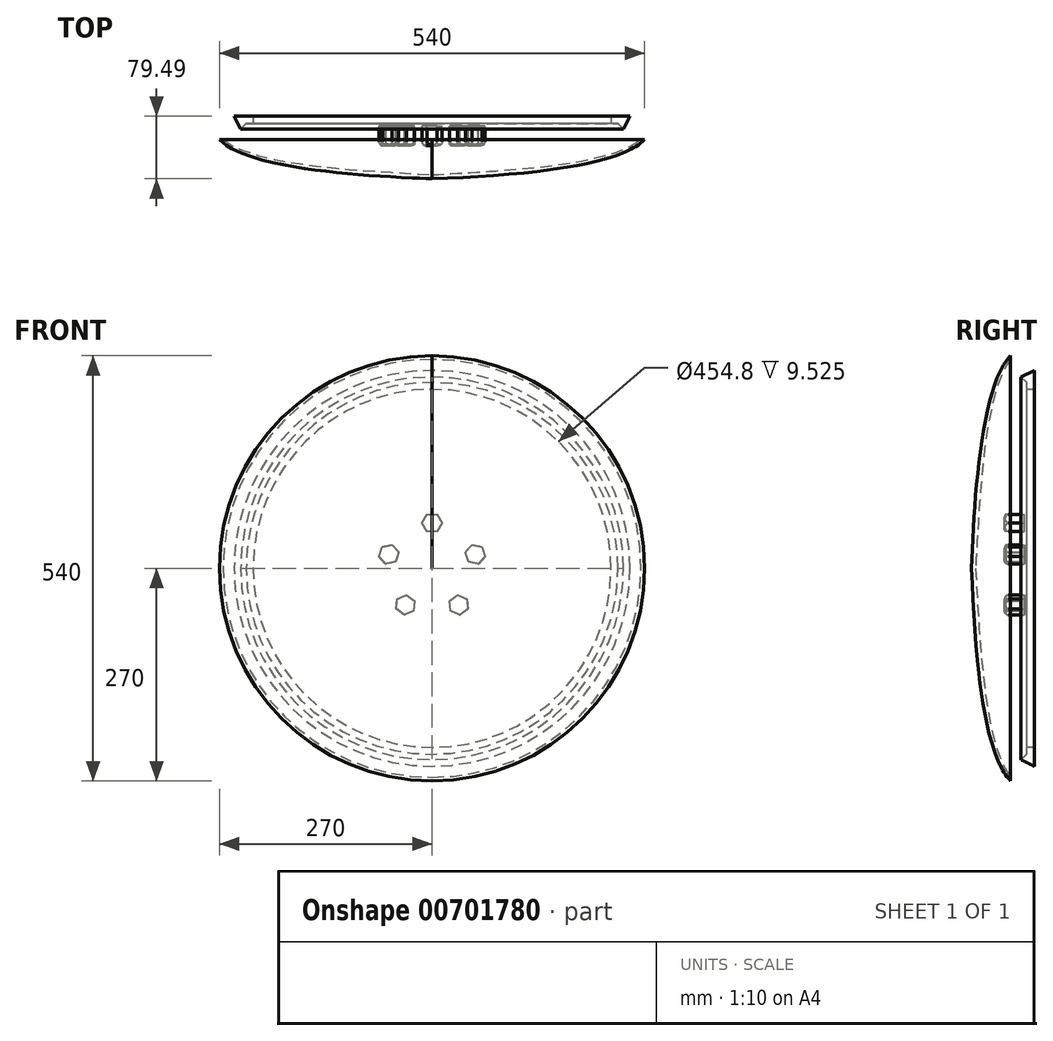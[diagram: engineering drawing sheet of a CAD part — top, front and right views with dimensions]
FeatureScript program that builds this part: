
annotation { "Feature Type Name" : "Feature", "Feature Type Description" : "" }
export const myFeature = defineFeature(function(context is Context, id is Id, definition is map)
    precondition{}
    {
        {
            var Q0;
            Q0=qCreatedBy(makeId("Right.planeOp"),FACE);
            var sketch = newSketch(context, id + "F0", { "sketchPlane" : qUnion([Q0])});
            skLineSegment(sketch, "E0", {"start": v(-492.36, 0) * mm, "end": v(495.3, 0) * mm, "construction": true});
            skLineSegment(sketch, "E1", {"start": v(0, 375.13) * mm, "end": v(0, -370.11) * mm, "construction": true});
            skLineSegment(sketch, "E2", {"start": v(-208.2, 270) * mm, "end": v(-199.87, 270) * mm});
            skLineSegment(sketch, "E3", {"start": v(-208.2, 270) * mm, "end": v(-208.2, 265.42) * mm});
            skLineSegment(sketch, "E4", {"start": v(-208.2, 265.42) * mm, "end": v(-200.05, 260.68) * mm});
            skLineSegment(sketch, "E5", {"start": v(-199.87, 270) * mm, "end": v(-187.28, 253.15) * mm});
            skLineSegment(sketch, "E6", {"start": v(-187.28, 253.15) * mm, "end": v(0, 253.15) * mm});
            skLineSegment(sketch, "E7", {"start": v(-200.05, 260.68) * mm, "end": v(-200.05, 247) * mm});
            skLineSegment(sketch, "E8", {"start": v(-200.05, 247) * mm, "end": v(-212.9, 237.4) * mm});
            skFitSpline(sketch, "E9", {"points": [v(-212.9, 237.4) * mm, v(-223.98, 98.87) * mm], "startDerivative": vector(-18.19, -11.12) * mm, "endDerivative": vector(-3.6, -383.35) * mm});
            skFitSpline(sketch, "E10", {"points": [v(-223.98, 98.87) * mm, v(-190, 0) * mm], "startDerivative": vector(-2.79, -53.63) * mm, "endDerivative": vector(-2.72, -261.66) * mm});
            skLineSegment(sketch, "E11", {"start": v(0, 245.77) * mm, "end": v(-188.8, 245.77) * mm});
            skFitSpline(sketch, "E12", {"points": [v(-188.8, 245.77) * mm, v(-188.8, 102.31) * mm], "startDerivative": vector(-99.7, -5.27) * mm, "endDerivative": vector(28.6, -46.07) * mm});
            skFitSpline(sketch, "E13", {"points": [v(-188.8, 102.31) * mm, v(-128.64, 85.7) * mm], "startDerivative": vector(31.05, -59.65) * mm, "endDerivative": vector(99.06, -4.24) * mm});
            skLineSegment(sketch, "E14.MirrorCS", {"start": v(187.28, 253.15) * mm, "end": v(0, 253.15) * mm});
            skLineSegment(sketch, "E15.MirrorCS", {"start": v(0, 245.77) * mm, "end": v(188.8, 245.77) * mm});
            skLineSegment(sketch, "E16.MirrorCS", {"start": v(199.87, 270) * mm, "end": v(187.28, 253.15) * mm});
            skLineSegment(sketch, "E17.MirrorCS", {"start": v(208.2, 270) * mm, "end": v(199.87, 270) * mm});
            skLineSegment(sketch, "E18.MirrorCS", {"start": v(208.2, 270) * mm, "end": v(208.2, 265.42) * mm});
            skLineSegment(sketch, "E19", {"start": v(208.2, 265.42) * mm, "end": v(192.74, 245.77) * mm});
            skLineSegment(sketch, "E20", {"start": v(192.74, 245.77) * mm, "end": v(188.8, 245.77) * mm});
            skLineSegment(sketch, "E21", {"start": v(-128.64, 85.7) * mm, "end": v(-128.64, 0) * mm});
            skLineSegment(sketch, "E22", {"start": v(-128.64, 0) * mm, "end": v(-190, 0) * mm});
            skSolve(sketch);
        }
        {
            var Q0;
            Q0 = qSketchRegion(id + "F0", true);
            var Q1;
            Q1=sQuery(id+"F0.wireOp",EDGE,"E0");
            revolve(context, id + "F1", {"entities" : qUnion([Q0]), "axis" : qUnion([Q1]), "revolveType" : RevolveType.FULL});
        }
        {
            var Q0;
            Q0=qCreatedBy(makeId("Front.planeOp"),FACE);
            cPlane(context, id + "F2", {"entities" : qUnion([Q0]), "cplaneType" : CPlaneType.OFFSET, "offset" : 230 * mm, "width" : 150 * mm, "height" : 150 * mm});
        }
        {
            var Q0;
            Q0=qCreatedBy(id+"F2.planeOp",FACE);
            var sketch = newSketch(context, id + "F3", { "sketchPlane" : qUnion([Q0])});
            skLineSegment(sketch, "E23", {"start": v(0, 0) * mm, "end": v(0, 316.28) * mm, "construction": true});
            skArc(sketch, "E24", {"start": v(-3.8, 244.37) * mm, "mid": v(-6.72, 170.75) * mm, "end": v(-5.1, 97.1) * mm});
            skArc(sketch, "E25.MirrorCS", {"start": v(3.8, 244.37) * mm, "mid": v(6.72, 170.75) * mm, "end": v(5.1, 97.1) * mm});
            skArc(sketch, "E26", {"start": v(3.8, 244.37) * mm, "mid": v(0, 248.44) * mm, "end": v(-3.8, 244.37) * mm});
            skArc(sketch, "E27", {"start": v(-5.1, 97.1) * mm, "mid": v(0, 92.54) * mm, "end": v(5.1, 97.1) * mm});
            skLineSegment(sketch, "E28", {"start": v(0, 0) * mm, "end": v(-180.56, 248.53) * mm, "construction": true});
            skArc(sketch, "E29", {"start": v(-147.8, 195.5) * mm, "mid": v(-103.99, 129.86) * mm, "end": v(-55.27, 67.78) * mm});
            skArc(sketch, "E30.MirrorCS", {"start": v(-140.25, 200.98) * mm, "mid": v(-91.37, 139.03) * mm, "end": v(-47.38, 73.51) * mm});
            skArc(sketch, "E31", {"start": v(-140.25, 200.98) * mm, "mid": v(-146.94, 202.25) * mm, "end": v(-147.8, 195.5) * mm});
            skArc(sketch, "E32", {"start": v(-55.27, 67.78) * mm, "mid": v(-48.36, 66.56) * mm, "end": v(-47.38, 73.51) * mm});
            skArc(sketch, "E33.1.0", {"start": v(-233.58, 71.9) * mm, "mid": v(-164.47, 46.37) * mm, "end": v(-93.93, 25.16) * mm});
            skArc(sketch, "E33.1.1", {"start": v(-231.23, 79.12) * mm, "mid": v(-236.28, 76.77) * mm, "end": v(-233.58, 71.9) * mm});
            skArc(sketch, "E33.1.2", {"start": v(-231.23, 79.12) * mm, "mid": v(-160.32, 59.16) * mm, "end": v(-90.77, 34.85) * mm});
            skArc(sketch, "E33.1.3", {"start": v(-93.93, 25.16) * mm, "mid": v(-88, 28.6) * mm, "end": v(-90.77, 34.85) * mm});
            skArc(sketch, "E33.1.4", {"start": v(-81.54, -31.62) * mm, "mid": v(-78.25, -25.42) * mm, "end": v(-84.56, -22.35) * mm});
            skArc(sketch, "E33.1.5", {"start": v(-231.6, -80.15) * mm, "mid": v(-155.64, -58.77) * mm, "end": v(-81.54, -31.62) * mm});
            skArc(sketch, "E33.1.6", {"start": v(-234.48, -71.28) * mm, "mid": v(-160.46, -43.94) * mm, "end": v(-84.56, -22.35) * mm});
            skArc(sketch, "E33.1.7", {"start": v(-234.48, -71.28) * mm, "mid": v(-237.76, -77.25) * mm, "end": v(-231.6, -80.15) * mm});
            skArc(sketch, "E33.2.0", {"start": v(-140.56, -199.93) * mm, "mid": v(-94.93, -142.1) * mm, "end": v(-52.95, -81.55) * mm});
            skArc(sketch, "E33.2.1", {"start": v(-146.7, -195.47) * mm, "mid": v(-146.03, -200.99) * mm, "end": v(-140.56, -199.93) * mm});
            skArc(sketch, "E33.2.2", {"start": v(-146.7, -195.47) * mm, "mid": v(-105.8, -134.2) * mm, "end": v(-61.2, -75.56) * mm});
            skArc(sketch, "E33.2.3", {"start": v(-52.95, -81.55) * mm, "mid": v(-54.4, -74.86) * mm, "end": v(-61.2, -75.56) * mm});
            skArc(sketch, "E33.2.4", {"start": v(4.88, -87.32) * mm, "mid": v(0, -82.28) * mm, "end": v(-4.88, -87.32) * mm});
            skArc(sketch, "E33.2.5", {"start": v(4.66, -245.03) * mm, "mid": v(7.8, -166.18) * mm, "end": v(4.88, -87.32) * mm});
            skArc(sketch, "E33.2.6", {"start": v(-4.66, -245.03) * mm, "mid": v(-7.8, -166.18) * mm, "end": v(-4.88, -87.32) * mm});
            skArc(sketch, "E33.2.7", {"start": v(-4.66, -245.03) * mm, "mid": v(0, -250) * mm, "end": v(4.66, -245.03) * mm});
            skArc(sketch, "E33.3.0", {"start": v(146.7, -195.47) * mm, "mid": v(105.8, -134.2) * mm, "end": v(61.2, -75.56) * mm});
            skArc(sketch, "E33.3.1", {"start": v(140.56, -199.93) * mm, "mid": v(146.03, -200.99) * mm, "end": v(146.7, -195.47) * mm});
            skArc(sketch, "E33.3.2", {"start": v(140.56, -199.93) * mm, "mid": v(94.93, -142.1) * mm, "end": v(52.95, -81.55) * mm});
            skArc(sketch, "E33.3.3", {"start": v(61.2, -75.56) * mm, "mid": v(54.4, -74.86) * mm, "end": v(52.95, -81.55) * mm});
            skArc(sketch, "E33.3.4", {"start": v(84.56, -22.35) * mm, "mid": v(78.25, -25.42) * mm, "end": v(81.54, -31.62) * mm});
            skArc(sketch, "E33.3.5", {"start": v(234.48, -71.28) * mm, "mid": v(160.46, -43.94) * mm, "end": v(84.56, -22.35) * mm});
            skArc(sketch, "E33.3.6", {"start": v(231.6, -80.15) * mm, "mid": v(155.64, -58.77) * mm, "end": v(81.54, -31.62) * mm});
            skArc(sketch, "E33.3.7", {"start": v(231.6, -80.15) * mm, "mid": v(237.76, -77.25) * mm, "end": v(234.48, -71.28) * mm});
            skArc(sketch, "E33.4.0", {"start": v(231.23, 79.12) * mm, "mid": v(160.32, 59.16) * mm, "end": v(90.77, 34.85) * mm});
            skArc(sketch, "E33.4.1", {"start": v(233.58, 71.9) * mm, "mid": v(236.28, 76.77) * mm, "end": v(231.23, 79.12) * mm});
            skArc(sketch, "E33.4.2", {"start": v(233.58, 71.9) * mm, "mid": v(164.47, 46.37) * mm, "end": v(93.93, 25.16) * mm});
            skArc(sketch, "E33.4.3", {"start": v(90.77, 34.85) * mm, "mid": v(88, 28.6) * mm, "end": v(93.93, 25.16) * mm});
            skArc(sketch, "E33.4.4", {"start": v(47.38, 73.51) * mm, "mid": v(48.36, 66.56) * mm, "end": v(55.27, 67.78) * mm});
            skArc(sketch, "E33.4.5", {"start": v(140.25, 200.98) * mm, "mid": v(91.37, 139.03) * mm, "end": v(47.38, 73.51) * mm});
            skArc(sketch, "E33.4.6", {"start": v(147.8, 195.5) * mm, "mid": v(103.99, 129.86) * mm, "end": v(55.27, 67.78) * mm});
            skArc(sketch, "E33.4.7", {"start": v(147.8, 195.5) * mm, "mid": v(146.94, 202.25) * mm, "end": v(140.25, 200.98) * mm});
            skPoint(sketch, "E33.center", {"position": v(0, 0) * mm});
            skSolve(sketch);
        }
        {
            var Q0;
            Q0 = qSketchRegion(id + "F3", true);
            extrude(context, id + "F4", {"entities" : qUnion([Q0]), "operationType" : NewBodyOperationType.REMOVE, "oppositeDirection" : true, "depth" : 46 * mm, "offsetDistance" : 25 * mm, "symmetric" : true});
        }
        {
            var Q0;
            Q0=qCreatedBy(makeId("Right.planeOp"),FACE);
            var sketch = newSketch(context, id + "F5", { "sketchPlane" : qUnion([Q0])});
            skFitSpline(sketch, "E34", {"points": [v(-219.3, 99.24) * mm, v(-211.26, 234.91) * mm], "startDerivative": vector(2.2, 123.97) * mm, "endDerivative": vector(26.33, 34.01) * mm});
            skLineSegment(sketch, "E35", {"start": v(-211.26, 234.91) * mm, "end": v(-194.07, 247.35) * mm});
            skFitSpline(sketch, "E36", {"points": [v(-219.3, 99.24) * mm, v(-188.84, 45.36) * mm], "startDerivative": vector(0.06, -33.78) * mm, "endDerivative": vector(11.74, -109.6) * mm});
            skFitSpline(sketch, "E37", {"points": [v(-188.84, 45.36) * mm, v(-194.07, 247.35) * mm], "startDerivative": vector(-5.23, 201.99) * mm, "endDerivative": vector(97.82, 84.09) * mm});
            skSolve(sketch);
        }
        {
            var Q0;
            Q0 = qSketchRegion(id + "F5", true);
            var Q1;
            Q1=sQuery(id+"F0.wireOp",EDGE,"E0");
            revolve(context, id + "F6", {"operationType" : NewBodyOperationType.ADD, "entities" : qUnion([Q0]), "axis" : qUnion([Q1]), "revolveType" : RevolveType.FULL});
        }
        {
            var Q0;
            Q0=makeQuery(id+"F1.opRevolve","SWEPT_FACE",FACE,{"disambiguationData":[OSD([sQuery(id+"F0.wireOp",EDGE,"E3")])]});
            var sketch = newSketch(context, id + "F7", { "sketchPlane" : qUnion([Q0])});
            skLineSegment(sketch, "E38", {"start": v(0, 0) * mm, "end": v(-101.12, 311.2) * mm, "construction": true});
            skLineSegment(sketch, "E39", {"start": v(0, 314.55) * mm, "end": v(0, -288.55) * mm, "construction": true});
            skArc(sketch, "E40", {"start": v(-118.5, 213.52) * mm, "mid": v(-123.32, 205.59) * mm, "end": v(-121.43, 196.51) * mm});
            skArc(sketch, "E41.MirrorCS", {"start": v(-29.63, 242.4) * mm, "mid": v(-21.08, 238.8) * mm, "end": v(-17.26, 230.36) * mm});
            skArc(sketch, "E42", {"start": v(-39.91, 91.58) * mm, "mid": v(-28.7, 88.34) * mm, "end": v(-21.54, 97.55) * mm});
            skArc(sketch, "E43", {"start": v(-118.5, 213.52) * mm, "mid": v(-75.46, 232.25) * mm, "end": v(-29.63, 242.4) * mm});
            skLineSegment(sketch, "E44", {"start": v(-121.43, 196.51) * mm, "end": v(-39.91, 91.58) * mm});
            skLineSegment(sketch, "E45", {"start": v(-17.26, 230.36) * mm, "end": v(-21.54, 97.55) * mm});
            skArc(sketch, "E46.1.0", {"start": v(-221.38, 103.08) * mm, "mid": v(-197.56, 143.54) * mm, "end": v(-166.45, 178.69) * mm});
            skArc(sketch, "E46.1.1", {"start": v(-166.45, 178.69) * mm, "mid": v(-157.42, 180.81) * mm, "end": v(-149.37, 176.22) * mm});
            skLineSegment(sketch, "E46.1.2", {"start": v(-149.37, 176.22) * mm, "end": v(-74.77, 66.26) * mm});
            skArc(sketch, "E46.1.3", {"start": v(-86.12, 50.63) * mm, "mid": v(-75.15, 54.6) * mm, "end": v(-74.77, 66.26) * mm});
            skLineSegment(sketch, "E46.1.4", {"start": v(-213.75, 87.6) * mm, "end": v(-86.12, 50.63) * mm});
            skArc(sketch, "E46.1.5", {"start": v(-221.38, 103.08) * mm, "mid": v(-220.6, 93.84) * mm, "end": v(-213.75, 87.6) * mm});
            skArc(sketch, "E46.2.0", {"start": v(-239.69, -46.73) * mm, "mid": v(-244.2, 0) * mm, "end": v(-239.69, 46.73) * mm});
            skArc(sketch, "E46.2.1", {"start": v(-239.69, 46.73) * mm, "mid": v(-233.63, 53.75) * mm, "end": v(-224.42, 54.77) * mm});
            skLineSegment(sketch, "E46.2.2", {"start": v(-224.42, 54.77) * mm, "end": v(-99.43, 9.66) * mm});
            skArc(sketch, "E46.2.3", {"start": v(-99.43, -9.66) * mm, "mid": v(-92.88, 0) * mm, "end": v(-99.43, 9.66) * mm});
            skLineSegment(sketch, "E46.2.4", {"start": v(-224.42, -54.77) * mm, "end": v(-99.43, -9.66) * mm});
            skArc(sketch, "E46.2.5", {"start": v(-239.69, -46.73) * mm, "mid": v(-233.63, -53.75) * mm, "end": v(-224.42, -54.77) * mm});
            skArc(sketch, "E46.3.0", {"start": v(-166.45, -178.69) * mm, "mid": v(-197.56, -143.54) * mm, "end": v(-221.38, -103.08) * mm});
            skArc(sketch, "E46.3.1", {"start": v(-221.38, -103.08) * mm, "mid": v(-220.6, -93.84) * mm, "end": v(-213.75, -87.6) * mm});
            skLineSegment(sketch, "E46.3.2", {"start": v(-213.75, -87.6) * mm, "end": v(-86.12, -50.63) * mm});
            skArc(sketch, "E46.3.3", {"start": v(-74.77, -66.26) * mm, "mid": v(-75.15, -54.6) * mm, "end": v(-86.12, -50.63) * mm});
            skLineSegment(sketch, "E46.3.4", {"start": v(-149.37, -176.22) * mm, "end": v(-74.77, -66.26) * mm});
            skArc(sketch, "E46.3.5", {"start": v(-166.45, -178.69) * mm, "mid": v(-157.42, -180.81) * mm, "end": v(-149.37, -176.22) * mm});
            skArc(sketch, "E46.4.0", {"start": v(-29.63, -242.4) * mm, "mid": v(-75.46, -232.25) * mm, "end": v(-118.5, -213.52) * mm});
            skArc(sketch, "E46.4.1", {"start": v(-118.5, -213.52) * mm, "mid": v(-123.32, -205.59) * mm, "end": v(-121.43, -196.51) * mm});
            skLineSegment(sketch, "E46.4.2", {"start": v(-121.43, -196.51) * mm, "end": v(-39.91, -91.58) * mm});
            skArc(sketch, "E46.4.3", {"start": v(-21.54, -97.55) * mm, "mid": v(-28.7, -88.34) * mm, "end": v(-39.91, -91.58) * mm});
            skLineSegment(sketch, "E46.4.4", {"start": v(-17.26, -230.36) * mm, "end": v(-21.54, -97.55) * mm});
            skArc(sketch, "E46.4.5", {"start": v(-29.63, -242.4) * mm, "mid": v(-21.08, -238.8) * mm, "end": v(-17.26, -230.36) * mm});
            skArc(sketch, "E46.5.0", {"start": v(118.5, -213.52) * mm, "mid": v(75.46, -232.25) * mm, "end": v(29.63, -242.4) * mm});
            skArc(sketch, "E46.5.1", {"start": v(29.63, -242.4) * mm, "mid": v(21.08, -238.8) * mm, "end": v(17.26, -230.36) * mm});
            skLineSegment(sketch, "E46.5.2", {"start": v(17.26, -230.36) * mm, "end": v(21.54, -97.55) * mm});
            skArc(sketch, "E46.5.3", {"start": v(39.91, -91.58) * mm, "mid": v(28.7, -88.34) * mm, "end": v(21.54, -97.55) * mm});
            skLineSegment(sketch, "E46.5.4", {"start": v(121.43, -196.51) * mm, "end": v(39.91, -91.58) * mm});
            skArc(sketch, "E46.5.5", {"start": v(118.5, -213.52) * mm, "mid": v(123.32, -205.59) * mm, "end": v(121.43, -196.51) * mm});
            skArc(sketch, "E46.6.0", {"start": v(221.38, -103.08) * mm, "mid": v(197.56, -143.54) * mm, "end": v(166.45, -178.69) * mm});
            skArc(sketch, "E46.6.1", {"start": v(166.45, -178.69) * mm, "mid": v(157.42, -180.81) * mm, "end": v(149.37, -176.22) * mm});
            skLineSegment(sketch, "E46.6.2", {"start": v(149.37, -176.22) * mm, "end": v(74.77, -66.26) * mm});
            skArc(sketch, "E46.6.3", {"start": v(86.12, -50.63) * mm, "mid": v(75.15, -54.6) * mm, "end": v(74.77, -66.26) * mm});
            skLineSegment(sketch, "E46.6.4", {"start": v(213.75, -87.6) * mm, "end": v(86.12, -50.63) * mm});
            skArc(sketch, "E46.6.5", {"start": v(221.38, -103.08) * mm, "mid": v(220.6, -93.84) * mm, "end": v(213.75, -87.6) * mm});
            skArc(sketch, "E46.7.0", {"start": v(239.69, 46.73) * mm, "mid": v(244.2, 0) * mm, "end": v(239.69, -46.73) * mm});
            skArc(sketch, "E46.7.1", {"start": v(239.69, -46.73) * mm, "mid": v(233.63, -53.75) * mm, "end": v(224.42, -54.77) * mm});
            skLineSegment(sketch, "E46.7.2", {"start": v(224.42, -54.77) * mm, "end": v(99.43, -9.66) * mm});
            skArc(sketch, "E46.7.3", {"start": v(99.43, 9.66) * mm, "mid": v(92.88, 0) * mm, "end": v(99.43, -9.66) * mm});
            skLineSegment(sketch, "E46.7.4", {"start": v(224.42, 54.77) * mm, "end": v(99.43, 9.66) * mm});
            skArc(sketch, "E46.7.5", {"start": v(239.69, 46.73) * mm, "mid": v(233.63, 53.75) * mm, "end": v(224.42, 54.77) * mm});
            skArc(sketch, "E46.8.0", {"start": v(166.45, 178.69) * mm, "mid": v(197.56, 143.54) * mm, "end": v(221.38, 103.08) * mm});
            skArc(sketch, "E46.8.1", {"start": v(221.38, 103.08) * mm, "mid": v(220.6, 93.84) * mm, "end": v(213.75, 87.6) * mm});
            skLineSegment(sketch, "E46.8.2", {"start": v(213.75, 87.6) * mm, "end": v(86.12, 50.63) * mm});
            skArc(sketch, "E46.8.3", {"start": v(74.77, 66.26) * mm, "mid": v(75.15, 54.6) * mm, "end": v(86.12, 50.63) * mm});
            skLineSegment(sketch, "E46.8.4", {"start": v(149.37, 176.22) * mm, "end": v(74.77, 66.26) * mm});
            skArc(sketch, "E46.8.5", {"start": v(166.45, 178.69) * mm, "mid": v(157.42, 180.81) * mm, "end": v(149.37, 176.22) * mm});
            skArc(sketch, "E46.9.0", {"start": v(29.63, 242.4) * mm, "mid": v(75.46, 232.25) * mm, "end": v(118.5, 213.52) * mm});
            skArc(sketch, "E46.9.1", {"start": v(118.5, 213.52) * mm, "mid": v(123.32, 205.59) * mm, "end": v(121.43, 196.51) * mm});
            skLineSegment(sketch, "E46.9.2", {"start": v(121.43, 196.51) * mm, "end": v(39.91, 91.58) * mm});
            skArc(sketch, "E46.9.3", {"start": v(21.54, 97.55) * mm, "mid": v(28.7, 88.34) * mm, "end": v(39.91, 91.58) * mm});
            skLineSegment(sketch, "E46.9.4", {"start": v(17.26, 230.36) * mm, "end": v(21.54, 97.55) * mm});
            skArc(sketch, "E46.9.5", {"start": v(29.63, 242.4) * mm, "mid": v(21.08, 238.8) * mm, "end": v(17.26, 230.36) * mm});
            skSolve(sketch);
        }
        {
            var Q0;
            Q0 = qSketchRegion(id + "F7", true);
            extrude(context, id + "F8", {"entities" : qUnion([Q0]), "operationType" : NewBodyOperationType.REMOVE, "oppositeDirection" : true, "depth" : 205 * mm, "offsetDistance" : 25 * mm, "symmetric" : true});
        }
        {
            var Q0;
            Q0=makeQuery(id+"F6.boolean.opBoolean","SPLIT",FACE,{"disambiguationData":[TD([makeQuery(id+"F4.boolean.opBoolean","COPY",FACE,{"derivedFrom":makeQuery(id+"F4.opExtrude","SWEPT_FACE",FACE,{"disambiguationData":[OSD([sQuery(id+"F3.wireOp",EDGE,"E33.3.0")])]})})])],"derivedFrom":makeQuery(id+"F6.opRevolve","SWEPT_FACE",FACE,{"disambiguationData":[OSD([sQuery(id+"F5.wireOp",EDGE,"E34")])]})});
            var Q1;
            Q1=makeQuery(id+"F6.boolean.opBoolean","SPLIT",FACE,{"disambiguationData":[TD([makeQuery(id+"F4.boolean.opBoolean","COPY",FACE,{"derivedFrom":makeQuery(id+"F4.opExtrude","SWEPT_FACE",FACE,{"disambiguationData":[OSD([sQuery(id+"F3.wireOp",EDGE,"E33.3.0")])]})})])],"derivedFrom":makeQuery(id+"F6.opRevolve","SWEPT_FACE",FACE,{"disambiguationData":[OSD([sQuery(id+"F5.wireOp",EDGE,"E36")])]})});
            var Q2;
            {var subQ0=sQuery(id+"F3.wireOp",EDGE,"E33.3.0");Q2=makeQuery(id+"F6.boolean.opBoolean","SPLIT",FACE,{"disambiguationData":[TD([makeQuery(id+"F4.boolean.opBoolean","COPY",FACE,{"derivedFrom":makeQuery(id+"F4.opExtrude","SWEPT_FACE",FACE,{"disambiguationData":[OSD([subQ0])]})})])],"derivedFrom":makeQuery(id+"F6.opRevolve","SWEPT_FACE",FACE,{"disambiguationData":[OSD([sQuery(id+"F5.wireOp",EDGE,"E35")])]})});}
            var Q3;
            Q3=makeQuery(id+"F6.boolean.opBoolean","SPLIT",FACE,{"disambiguationData":[TD([makeQuery(id+"F4.boolean.opBoolean","COPY",FACE,{"derivedFrom":makeQuery(id+"F4.opExtrude","SWEPT_FACE",FACE,{"disambiguationData":[OSD([sQuery(id+"F3.wireOp",EDGE,"E33.4.0")])]})})])],"derivedFrom":makeQuery(id+"F6.opRevolve","SWEPT_FACE",FACE,{"disambiguationData":[OSD([sQuery(id+"F5.wireOp",EDGE,"E36")])]})});
            var Q4;
            Q4=makeQuery(id+"F6.boolean.opBoolean","SPLIT",FACE,{"disambiguationData":[TD([makeQuery(id+"F4.boolean.opBoolean","COPY",FACE,{"derivedFrom":makeQuery(id+"F4.opExtrude","SWEPT_FACE",FACE,{"disambiguationData":[OSD([sQuery(id+"F3.wireOp",EDGE,"E33.4.0")])]})})])],"derivedFrom":makeQuery(id+"F6.opRevolve","SWEPT_FACE",FACE,{"disambiguationData":[OSD([sQuery(id+"F5.wireOp",EDGE,"E34")])]})});
            var Q5;
            {var subQ0=sQuery(id+"F3.wireOp",EDGE,"E33.4.0");Q5=makeQuery(id+"F6.boolean.opBoolean","SPLIT",FACE,{"disambiguationData":[TD([makeQuery(id+"F4.boolean.opBoolean","COPY",FACE,{"derivedFrom":makeQuery(id+"F4.opExtrude","SWEPT_FACE",FACE,{"disambiguationData":[OSD([subQ0])]})})])],"derivedFrom":makeQuery(id+"F6.opRevolve","SWEPT_FACE",FACE,{"disambiguationData":[OSD([sQuery(id+"F5.wireOp",EDGE,"E35")])]})});}
            var Q6;
            Q6=makeQuery(id+"F6.boolean.opBoolean","SPLIT",FACE,{"disambiguationData":[TD([makeQuery(id+"F4.boolean.opBoolean","COPY",FACE,{"derivedFrom":makeQuery(id+"F4.opExtrude","SWEPT_FACE",FACE,{"disambiguationData":[OSD([sQuery(id+"F3.wireOp",EDGE,"E24")])]})})])],"derivedFrom":makeQuery(id+"F6.opRevolve","SWEPT_FACE",FACE,{"disambiguationData":[OSD([sQuery(id+"F5.wireOp",EDGE,"E36")])]})});
            var Q7;
            Q7=makeQuery(id+"F6.boolean.opBoolean","SPLIT",FACE,{"disambiguationData":[TD([makeQuery(id+"F4.boolean.opBoolean","COPY",FACE,{"derivedFrom":makeQuery(id+"F4.opExtrude","SWEPT_FACE",FACE,{"disambiguationData":[OSD([sQuery(id+"F3.wireOp",EDGE,"E24")])]})})])],"derivedFrom":makeQuery(id+"F6.opRevolve","SWEPT_FACE",FACE,{"disambiguationData":[OSD([sQuery(id+"F5.wireOp",EDGE,"E34")])]})});
            var Q8;
            Q8=makeQuery(id+"F6.boolean.opBoolean","SPLIT",FACE,{"disambiguationData":[TD([makeQuery(id+"F4.boolean.opBoolean","COPY",FACE,{"derivedFrom":makeQuery(id+"F4.opExtrude","SWEPT_FACE",FACE,{"disambiguationData":[OSD([sQuery(id+"F3.wireOp",EDGE,"E33.1.0")])]})})])],"derivedFrom":makeQuery(id+"F6.opRevolve","SWEPT_FACE",FACE,{"disambiguationData":[OSD([sQuery(id+"F5.wireOp",EDGE,"E36")])]})});
            var Q9;
            Q9=makeQuery(id+"F6.boolean.opBoolean","SPLIT",FACE,{"disambiguationData":[TD([makeQuery(id+"F4.boolean.opBoolean","COPY",FACE,{"derivedFrom":makeQuery(id+"F4.opExtrude","SWEPT_FACE",FACE,{"disambiguationData":[OSD([sQuery(id+"F3.wireOp",EDGE,"E33.1.0")])]})})])],"derivedFrom":makeQuery(id+"F6.opRevolve","SWEPT_FACE",FACE,{"disambiguationData":[OSD([sQuery(id+"F5.wireOp",EDGE,"E34")])]})});
            var Q10;
            {var subQ0=sQuery(id+"F3.wireOp",EDGE,"E33.1.0");Q10=makeQuery(id+"F6.boolean.opBoolean","SPLIT",FACE,{"disambiguationData":[TD([makeQuery(id+"F4.boolean.opBoolean","COPY",FACE,{"derivedFrom":makeQuery(id+"F4.opExtrude","SWEPT_FACE",FACE,{"disambiguationData":[OSD([subQ0])]})})])],"derivedFrom":makeQuery(id+"F6.opRevolve","SWEPT_FACE",FACE,{"disambiguationData":[OSD([sQuery(id+"F5.wireOp",EDGE,"E35")])]})});}
            var Q11;
            {var subQ0=sQuery(id+"F3.wireOp",EDGE,"E24");Q11=makeQuery(id+"F6.boolean.opBoolean","SPLIT",FACE,{"disambiguationData":[TD([makeQuery(id+"F4.boolean.opBoolean","COPY",FACE,{"derivedFrom":makeQuery(id+"F4.opExtrude","SWEPT_FACE",FACE,{"disambiguationData":[OSD([subQ0])]})})])],"derivedFrom":makeQuery(id+"F6.opRevolve","SWEPT_FACE",FACE,{"disambiguationData":[OSD([sQuery(id+"F5.wireOp",EDGE,"E35")])]})});}
            var Q12;
            Q12=makeQuery(id+"F6.boolean.opBoolean","SPLIT",FACE,{"disambiguationData":[TD([makeQuery(id+"F4.boolean.opBoolean","COPY",FACE,{"derivedFrom":makeQuery(id+"F4.opExtrude","SWEPT_FACE",FACE,{"disambiguationData":[OSD([sQuery(id+"F3.wireOp",EDGE,"E33.2.0")])]})})])],"derivedFrom":makeQuery(id+"F6.opRevolve","SWEPT_FACE",FACE,{"disambiguationData":[OSD([sQuery(id+"F5.wireOp",EDGE,"E36")])]})});
            var Q13;
            Q13=makeQuery(id+"F6.boolean.opBoolean","SPLIT",FACE,{"disambiguationData":[TD([makeQuery(id+"F4.boolean.opBoolean","COPY",FACE,{"derivedFrom":makeQuery(id+"F4.opExtrude","SWEPT_FACE",FACE,{"disambiguationData":[OSD([sQuery(id+"F3.wireOp",EDGE,"E33.2.0")])]})})])],"derivedFrom":makeQuery(id+"F6.opRevolve","SWEPT_FACE",FACE,{"disambiguationData":[OSD([sQuery(id+"F5.wireOp",EDGE,"E34")])]})});
            var Q14;
            {var subQ0=sQuery(id+"F3.wireOp",EDGE,"E33.2.0");Q14=makeQuery(id+"F6.boolean.opBoolean","SPLIT",FACE,{"disambiguationData":[TD([makeQuery(id+"F4.boolean.opBoolean","COPY",FACE,{"derivedFrom":makeQuery(id+"F4.opExtrude","SWEPT_FACE",FACE,{"disambiguationData":[OSD([subQ0])]})})])],"derivedFrom":makeQuery(id+"F6.opRevolve","SWEPT_FACE",FACE,{"disambiguationData":[OSD([sQuery(id+"F5.wireOp",EDGE,"E35")])]})});}
            fillet(context, id + "F9", {"entities" : qUnion([Q0, Q1, Q2, Q3, Q4, Q5, Q6, Q7, Q8, Q9, Q10, Q11, Q12, Q13, Q14]), "radius" : 2.5 * mm, "tangentPropagation" : true, "allowEdgeOverflow" : false});
        }
        {
            var Q0;
            Q0=makeQuery(id+"F6.boolean.opBoolean","INTERSECT",EDGE,{"derivedFrom":[makeQuery(id+"F4.boolean.opBoolean","COPY",FACE,{"derivedFrom":makeQuery(id+"F4.opExtrude","SWEPT_FACE",FACE,{"disambiguationData":[OSD([sQuery(id+"F3.wireOp",EDGE,"E33.4.6")])]})}),makeQuery(id+"F6.opRevolve","SWEPT_FACE",FACE,{"disambiguationData":[OSD([sQuery(id+"F5.wireOp",EDGE,"E34")])]})]});
            var Q1;
            Q1=makeQuery(id+"F6.boolean.opBoolean","INTERSECT",EDGE,{"derivedFrom":[makeQuery(id+"F4.boolean.opBoolean","COPY",FACE,{"derivedFrom":makeQuery(id+"F4.opExtrude","SWEPT_FACE",FACE,{"disambiguationData":[OSD([sQuery(id+"F3.wireOp",EDGE,"E33.4.6")])]})}),makeQuery(id+"F6.opRevolve","SWEPT_FACE",FACE,{"disambiguationData":[OSD([sQuery(id+"F5.wireOp",EDGE,"E36")])]})]});
            var Q2;
            Q2=makeQuery(id+"F6.boolean.opBoolean","INTERSECT",EDGE,{"disambiguationData":[OD(1.0)],"derivedFrom":[makeQuery(id+"F4.boolean.opBoolean","COPY",FACE,{"derivedFrom":makeQuery(id+"F4.opExtrude","SWEPT_FACE",FACE,{"disambiguationData":[OSD([sQuery(id+"F3.wireOp",EDGE,"E33.4.4")])]})}),makeQuery(id+"F6.opRevolve","SWEPT_FACE",FACE,{"disambiguationData":[OSD([sQuery(id+"F5.wireOp",EDGE,"E36")])]})]});
            var Q3;
            Q3=makeQuery(id+"F6.boolean.opBoolean","INTERSECT",EDGE,{"disambiguationData":[OD(0.0)],"derivedFrom":[makeQuery(id+"F4.boolean.opBoolean","COPY",FACE,{"derivedFrom":makeQuery(id+"F4.opExtrude","SWEPT_FACE",FACE,{"disambiguationData":[OSD([sQuery(id+"F3.wireOp",EDGE,"E33.4.4")])]})}),makeQuery(id+"F6.opRevolve","SWEPT_FACE",FACE,{"disambiguationData":[OSD([sQuery(id+"F5.wireOp",EDGE,"E36")])]})]});
            var Q4;
            Q4=makeQuery(id+"F6.boolean.opBoolean","INTERSECT",EDGE,{"derivedFrom":[makeQuery(id+"F4.boolean.opBoolean","COPY",FACE,{"derivedFrom":makeQuery(id+"F4.opExtrude","SWEPT_FACE",FACE,{"disambiguationData":[OSD([sQuery(id+"F3.wireOp",EDGE,"E33.4.5")])]})}),makeQuery(id+"F6.opRevolve","SWEPT_FACE",FACE,{"disambiguationData":[OSD([sQuery(id+"F5.wireOp",EDGE,"E36")])]})]});
            var Q5;
            Q5=makeQuery(id+"F6.boolean.opBoolean","INTERSECT",EDGE,{"derivedFrom":[makeQuery(id+"F4.boolean.opBoolean","COPY",FACE,{"derivedFrom":makeQuery(id+"F4.opExtrude","SWEPT_FACE",FACE,{"disambiguationData":[OSD([sQuery(id+"F3.wireOp",EDGE,"E33.4.5")])]})}),makeQuery(id+"F6.opRevolve","SWEPT_FACE",FACE,{"disambiguationData":[OSD([sQuery(id+"F5.wireOp",EDGE,"E34")])]})]});
            var Q6;
            Q6=makeQuery(id+"F6.boolean.opBoolean","INTERSECT",EDGE,{"derivedFrom":[makeQuery(id+"F4.boolean.opBoolean","COPY",FACE,{"derivedFrom":makeQuery(id+"F4.opExtrude","SWEPT_FACE",FACE,{"disambiguationData":[OSD([sQuery(id+"F3.wireOp",EDGE,"E33.4.5")])]})}),makeQuery(id+"F6.opRevolve","SWEPT_FACE",FACE,{"disambiguationData":[OSD([sQuery(id+"F5.wireOp",EDGE,"E35")])]})]});
            var Q7;
            Q7=makeQuery(id+"F6.boolean.opBoolean","INTERSECT",EDGE,{"derivedFrom":[makeQuery(id+"F4.boolean.opBoolean","COPY",FACE,{"derivedFrom":makeQuery(id+"F4.opExtrude","SWEPT_FACE",FACE,{"disambiguationData":[OSD([sQuery(id+"F3.wireOp",EDGE,"E33.4.6")])]})}),makeQuery(id+"F6.opRevolve","SWEPT_FACE",FACE,{"disambiguationData":[OSD([sQuery(id+"F5.wireOp",EDGE,"E35")])]})]});
            var Q8;
            Q8=makeQuery(id+"F6.boolean.opBoolean","INTERSECT",EDGE,{"derivedFrom":[makeQuery(id+"F4.boolean.opBoolean","COPY",FACE,{"derivedFrom":makeQuery(id+"F4.opExtrude","CAP_FACE",FACE,{"disambiguationData":[OSD([sQuery(id+"F3.wireOp",EDGE,"E33.4.4"),sQuery(id+"F3.wireOp",EDGE,"E33.4.5"),sQuery(id+"F3.wireOp",EDGE,"E33.4.6"),sQuery(id+"F3.wireOp",EDGE,"E33.4.7")])],"isStart":false})}),makeQuery(id+"F6.opRevolve","SWEPT_FACE",FACE,{"disambiguationData":[OSD([sQuery(id+"F5.wireOp",EDGE,"E35")])]})]});
            var Q9;
            Q9=makeQuery(id+"F4.boolean.opBoolean","COPY",EDGE,{"derivedFrom":makeQuery(id+"F4.opExtrude","CAP_EDGE",EDGE,{"disambiguationData":[OSD([sQuery(id+"F3.wireOp",EDGE,"E33.4.4")])],"isStart":false})});
            var Q10;
            Q10=makeQuery(id+"F6.boolean.opBoolean","INTERSECT",EDGE,{"derivedFrom":[makeQuery(id+"F4.boolean.opBoolean","COPY",FACE,{"derivedFrom":makeQuery(id+"F4.opExtrude","SWEPT_FACE",FACE,{"disambiguationData":[OSD([sQuery(id+"F3.wireOp",EDGE,"E30.MirrorCS")])]})}),makeQuery(id+"F6.opRevolve","SWEPT_FACE",FACE,{"disambiguationData":[OSD([sQuery(id+"F5.wireOp",EDGE,"E35")])]})]});
            var Q11;
            Q11=makeQuery(id+"F6.boolean.opBoolean","INTERSECT",EDGE,{"derivedFrom":[makeQuery(id+"F4.boolean.opBoolean","COPY",FACE,{"derivedFrom":makeQuery(id+"F4.opExtrude","SWEPT_FACE",FACE,{"disambiguationData":[OSD([sQuery(id+"F3.wireOp",EDGE,"E30.MirrorCS")])]})}),makeQuery(id+"F6.opRevolve","SWEPT_FACE",FACE,{"disambiguationData":[OSD([sQuery(id+"F5.wireOp",EDGE,"E34")])]})]});
            var Q12;
            Q12=makeQuery(id+"F6.boolean.opBoolean","INTERSECT",EDGE,{"derivedFrom":[makeQuery(id+"F4.boolean.opBoolean","COPY",FACE,{"derivedFrom":makeQuery(id+"F4.opExtrude","SWEPT_FACE",FACE,{"disambiguationData":[OSD([sQuery(id+"F3.wireOp",EDGE,"E30.MirrorCS")])]})}),makeQuery(id+"F6.opRevolve","SWEPT_FACE",FACE,{"disambiguationData":[OSD([sQuery(id+"F5.wireOp",EDGE,"E36")])]})]});
            var Q13;
            Q13=makeQuery(id+"F6.boolean.opBoolean","INTERSECT",EDGE,{"disambiguationData":[OD(1.0)],"derivedFrom":[makeQuery(id+"F4.boolean.opBoolean","COPY",FACE,{"derivedFrom":makeQuery(id+"F4.opExtrude","SWEPT_FACE",FACE,{"disambiguationData":[OSD([sQuery(id+"F3.wireOp",EDGE,"E32")])]})}),makeQuery(id+"F6.opRevolve","SWEPT_FACE",FACE,{"disambiguationData":[OSD([sQuery(id+"F5.wireOp",EDGE,"E36")])]})]});
            var Q14;
            Q14=makeQuery(id+"F6.boolean.opBoolean","INTERSECT",EDGE,{"derivedFrom":[makeQuery(id+"F4.boolean.opBoolean","COPY",FACE,{"derivedFrom":makeQuery(id+"F4.opExtrude","SWEPT_FACE",FACE,{"disambiguationData":[OSD([sQuery(id+"F3.wireOp",EDGE,"E29")])]})}),makeQuery(id+"F6.opRevolve","SWEPT_FACE",FACE,{"disambiguationData":[OSD([sQuery(id+"F5.wireOp",EDGE,"E36")])]})]});
            var Q15;
            Q15=makeQuery(id+"F4.boolean.opBoolean","COPY",EDGE,{"derivedFrom":makeQuery(id+"F4.opExtrude","CAP_EDGE",EDGE,{"disambiguationData":[OSD([sQuery(id+"F3.wireOp",EDGE,"E32")])],"isStart":false})});
            var Q16;
            Q16=makeQuery(id+"F6.boolean.opBoolean","INTERSECT",EDGE,{"disambiguationData":[OD(0.0)],"derivedFrom":[makeQuery(id+"F4.boolean.opBoolean","COPY",FACE,{"derivedFrom":makeQuery(id+"F4.opExtrude","SWEPT_FACE",FACE,{"disambiguationData":[OSD([sQuery(id+"F3.wireOp",EDGE,"E32")])]})}),makeQuery(id+"F6.opRevolve","SWEPT_FACE",FACE,{"disambiguationData":[OSD([sQuery(id+"F5.wireOp",EDGE,"E36")])]})]});
            var Q17;
            Q17=makeQuery(id+"F6.boolean.opBoolean","INTERSECT",EDGE,{"derivedFrom":[makeQuery(id+"F4.boolean.opBoolean","COPY",FACE,{"derivedFrom":makeQuery(id+"F4.opExtrude","SWEPT_FACE",FACE,{"disambiguationData":[OSD([sQuery(id+"F3.wireOp",EDGE,"E29")])]})}),makeQuery(id+"F6.opRevolve","SWEPT_FACE",FACE,{"disambiguationData":[OSD([sQuery(id+"F5.wireOp",EDGE,"E34")])]})]});
            var Q18;
            Q18=makeQuery(id+"F6.boolean.opBoolean","INTERSECT",EDGE,{"derivedFrom":[makeQuery(id+"F4.boolean.opBoolean","COPY",FACE,{"derivedFrom":makeQuery(id+"F4.opExtrude","SWEPT_FACE",FACE,{"disambiguationData":[OSD([sQuery(id+"F3.wireOp",EDGE,"E29")])]})}),makeQuery(id+"F6.opRevolve","SWEPT_FACE",FACE,{"disambiguationData":[OSD([sQuery(id+"F5.wireOp",EDGE,"E35")])]})]});
            var Q19;
            Q19=makeQuery(id+"F6.boolean.opBoolean","INTERSECT",EDGE,{"derivedFrom":[makeQuery(id+"F4.boolean.opBoolean","COPY",FACE,{"derivedFrom":makeQuery(id+"F4.opExtrude","CAP_FACE",FACE,{"disambiguationData":[OSD([sQuery(id+"F3.wireOp",EDGE,"E29"),sQuery(id+"F3.wireOp",EDGE,"E30.MirrorCS"),sQuery(id+"F3.wireOp",EDGE,"E31"),sQuery(id+"F3.wireOp",EDGE,"E32")])],"isStart":false})}),makeQuery(id+"F6.opRevolve","SWEPT_FACE",FACE,{"disambiguationData":[OSD([sQuery(id+"F5.wireOp",EDGE,"E35")])]})]});
            var Q20;
            Q20=makeQuery(id+"F6.boolean.opBoolean","INTERSECT",EDGE,{"derivedFrom":[makeQuery(id+"F4.boolean.opBoolean","COPY",FACE,{"derivedFrom":makeQuery(id+"F4.opExtrude","CAP_FACE",FACE,{"disambiguationData":[OSD([sQuery(id+"F3.wireOp",EDGE,"E33.1.4"),sQuery(id+"F3.wireOp",EDGE,"E33.1.5"),sQuery(id+"F3.wireOp",EDGE,"E33.1.6"),sQuery(id+"F3.wireOp",EDGE,"E33.1.7")])],"isStart":false})}),makeQuery(id+"F6.opRevolve","SWEPT_FACE",FACE,{"disambiguationData":[OSD([sQuery(id+"F5.wireOp",EDGE,"E35")])]})]});
            var Q21;
            Q21=makeQuery(id+"F6.boolean.opBoolean","INTERSECT",EDGE,{"derivedFrom":[makeQuery(id+"F4.boolean.opBoolean","COPY",FACE,{"derivedFrom":makeQuery(id+"F4.opExtrude","SWEPT_FACE",FACE,{"disambiguationData":[OSD([sQuery(id+"F3.wireOp",EDGE,"E33.1.6")])]})}),makeQuery(id+"F6.opRevolve","SWEPT_FACE",FACE,{"disambiguationData":[OSD([sQuery(id+"F5.wireOp",EDGE,"E35")])]})]});
            var Q22;
            Q22=makeQuery(id+"F6.boolean.opBoolean","INTERSECT",EDGE,{"derivedFrom":[makeQuery(id+"F4.boolean.opBoolean","COPY",FACE,{"derivedFrom":makeQuery(id+"F4.opExtrude","SWEPT_FACE",FACE,{"disambiguationData":[OSD([sQuery(id+"F3.wireOp",EDGE,"E33.1.6")])]})}),makeQuery(id+"F6.opRevolve","SWEPT_FACE",FACE,{"disambiguationData":[OSD([sQuery(id+"F5.wireOp",EDGE,"E34")])]})]});
            var Q23;
            Q23=makeQuery(id+"F6.boolean.opBoolean","INTERSECT",EDGE,{"derivedFrom":[makeQuery(id+"F4.boolean.opBoolean","COPY",FACE,{"derivedFrom":makeQuery(id+"F4.opExtrude","SWEPT_FACE",FACE,{"disambiguationData":[OSD([sQuery(id+"F3.wireOp",EDGE,"E33.1.6")])]})}),makeQuery(id+"F6.opRevolve","SWEPT_FACE",FACE,{"disambiguationData":[OSD([sQuery(id+"F5.wireOp",EDGE,"E36")])]})]});
            var Q24;
            Q24=makeQuery(id+"F6.boolean.opBoolean","INTERSECT",EDGE,{"disambiguationData":[OD(1.0)],"derivedFrom":[makeQuery(id+"F4.boolean.opBoolean","COPY",FACE,{"derivedFrom":makeQuery(id+"F4.opExtrude","SWEPT_FACE",FACE,{"disambiguationData":[OSD([sQuery(id+"F3.wireOp",EDGE,"E33.1.4")])]})}),makeQuery(id+"F6.opRevolve","SWEPT_FACE",FACE,{"disambiguationData":[OSD([sQuery(id+"F5.wireOp",EDGE,"E36")])]})]});
            var Q25;
            Q25=makeQuery(id+"F6.boolean.opBoolean","INTERSECT",EDGE,{"derivedFrom":[makeQuery(id+"F4.boolean.opBoolean","COPY",FACE,{"derivedFrom":makeQuery(id+"F4.opExtrude","SWEPT_FACE",FACE,{"disambiguationData":[OSD([sQuery(id+"F3.wireOp",EDGE,"E33.1.5")])]})}),makeQuery(id+"F6.opRevolve","SWEPT_FACE",FACE,{"disambiguationData":[OSD([sQuery(id+"F5.wireOp",EDGE,"E35")])]})]});
            var Q26;
            Q26=makeQuery(id+"F6.boolean.opBoolean","INTERSECT",EDGE,{"derivedFrom":[makeQuery(id+"F4.boolean.opBoolean","COPY",FACE,{"derivedFrom":makeQuery(id+"F4.opExtrude","SWEPT_FACE",FACE,{"disambiguationData":[OSD([sQuery(id+"F3.wireOp",EDGE,"E33.1.5")])]})}),makeQuery(id+"F6.opRevolve","SWEPT_FACE",FACE,{"disambiguationData":[OSD([sQuery(id+"F5.wireOp",EDGE,"E34")])]})]});
            var Q27;
            Q27=makeQuery(id+"F6.boolean.opBoolean","INTERSECT",EDGE,{"derivedFrom":[makeQuery(id+"F4.boolean.opBoolean","COPY",FACE,{"derivedFrom":makeQuery(id+"F4.opExtrude","SWEPT_FACE",FACE,{"disambiguationData":[OSD([sQuery(id+"F3.wireOp",EDGE,"E33.1.5")])]})}),makeQuery(id+"F6.opRevolve","SWEPT_FACE",FACE,{"disambiguationData":[OSD([sQuery(id+"F5.wireOp",EDGE,"E36")])]})]});
            var Q28;
            Q28=makeQuery(id+"F6.boolean.opBoolean","INTERSECT",EDGE,{"disambiguationData":[OD(0.0)],"derivedFrom":[makeQuery(id+"F4.boolean.opBoolean","COPY",FACE,{"derivedFrom":makeQuery(id+"F4.opExtrude","SWEPT_FACE",FACE,{"disambiguationData":[OSD([sQuery(id+"F3.wireOp",EDGE,"E33.1.4")])]})}),makeQuery(id+"F6.opRevolve","SWEPT_FACE",FACE,{"disambiguationData":[OSD([sQuery(id+"F5.wireOp",EDGE,"E36")])]})]});
            var Q29;
            Q29=makeQuery(id+"F4.boolean.opBoolean","COPY",EDGE,{"derivedFrom":makeQuery(id+"F4.opExtrude","CAP_EDGE",EDGE,{"disambiguationData":[OSD([sQuery(id+"F3.wireOp",EDGE,"E33.1.4")])],"isStart":false})});
            var Q30;
            Q30=makeQuery(id+"F6.boolean.opBoolean","INTERSECT",EDGE,{"disambiguationData":[OD(1.0)],"derivedFrom":[makeQuery(id+"F4.boolean.opBoolean","COPY",FACE,{"derivedFrom":makeQuery(id+"F4.opExtrude","SWEPT_FACE",FACE,{"disambiguationData":[OSD([sQuery(id+"F3.wireOp",EDGE,"E33.2.4")])]})}),makeQuery(id+"F6.opRevolve","SWEPT_FACE",FACE,{"disambiguationData":[OSD([sQuery(id+"F5.wireOp",EDGE,"E36")])]})]});
            var Q31;
            Q31=makeQuery(id+"F6.boolean.opBoolean","INTERSECT",EDGE,{"derivedFrom":[makeQuery(id+"F4.boolean.opBoolean","COPY",FACE,{"derivedFrom":makeQuery(id+"F4.opExtrude","SWEPT_FACE",FACE,{"disambiguationData":[OSD([sQuery(id+"F3.wireOp",EDGE,"E33.2.6")])]})}),makeQuery(id+"F6.opRevolve","SWEPT_FACE",FACE,{"disambiguationData":[OSD([sQuery(id+"F5.wireOp",EDGE,"E36")])]})]});
            var Q32;
            Q32=makeQuery(id+"F6.boolean.opBoolean","INTERSECT",EDGE,{"derivedFrom":[makeQuery(id+"F4.boolean.opBoolean","COPY",FACE,{"derivedFrom":makeQuery(id+"F4.opExtrude","SWEPT_FACE",FACE,{"disambiguationData":[OSD([sQuery(id+"F3.wireOp",EDGE,"E33.2.6")])]})}),makeQuery(id+"F6.opRevolve","SWEPT_FACE",FACE,{"disambiguationData":[OSD([sQuery(id+"F5.wireOp",EDGE,"E34")])]})]});
            var Q33;
            Q33=makeQuery(id+"F4.boolean.opBoolean","COPY",EDGE,{"derivedFrom":makeQuery(id+"F4.opExtrude","CAP_EDGE",EDGE,{"disambiguationData":[OSD([sQuery(id+"F3.wireOp",EDGE,"E33.2.4")])],"isStart":false})});
            var Q34;
            Q34=makeQuery(id+"F6.boolean.opBoolean","INTERSECT",EDGE,{"disambiguationData":[OD(0.0)],"derivedFrom":[makeQuery(id+"F4.boolean.opBoolean","COPY",FACE,{"derivedFrom":makeQuery(id+"F4.opExtrude","SWEPT_FACE",FACE,{"disambiguationData":[OSD([sQuery(id+"F3.wireOp",EDGE,"E33.2.4")])]})}),makeQuery(id+"F6.opRevolve","SWEPT_FACE",FACE,{"disambiguationData":[OSD([sQuery(id+"F5.wireOp",EDGE,"E36")])]})]});
            var Q35;
            Q35=makeQuery(id+"F6.boolean.opBoolean","INTERSECT",EDGE,{"derivedFrom":[makeQuery(id+"F4.boolean.opBoolean","COPY",FACE,{"derivedFrom":makeQuery(id+"F4.opExtrude","SWEPT_FACE",FACE,{"disambiguationData":[OSD([sQuery(id+"F3.wireOp",EDGE,"E33.2.5")])]})}),makeQuery(id+"F6.opRevolve","SWEPT_FACE",FACE,{"disambiguationData":[OSD([sQuery(id+"F5.wireOp",EDGE,"E36")])]})]});
            var Q36;
            Q36=makeQuery(id+"F6.boolean.opBoolean","INTERSECT",EDGE,{"derivedFrom":[makeQuery(id+"F4.boolean.opBoolean","COPY",FACE,{"derivedFrom":makeQuery(id+"F4.opExtrude","SWEPT_FACE",FACE,{"disambiguationData":[OSD([sQuery(id+"F3.wireOp",EDGE,"E33.2.5")])]})}),makeQuery(id+"F6.opRevolve","SWEPT_FACE",FACE,{"disambiguationData":[OSD([sQuery(id+"F5.wireOp",EDGE,"E34")])]})]});
            var Q37;
            Q37=makeQuery(id+"F6.boolean.opBoolean","INTERSECT",EDGE,{"derivedFrom":[makeQuery(id+"F4.boolean.opBoolean","COPY",FACE,{"derivedFrom":makeQuery(id+"F4.opExtrude","SWEPT_FACE",FACE,{"disambiguationData":[OSD([sQuery(id+"F3.wireOp",EDGE,"E33.2.5")])]})}),makeQuery(id+"F6.opRevolve","SWEPT_FACE",FACE,{"disambiguationData":[OSD([sQuery(id+"F5.wireOp",EDGE,"E35")])]})]});
            var Q38;
            Q38=makeQuery(id+"F6.boolean.opBoolean","INTERSECT",EDGE,{"derivedFrom":[makeQuery(id+"F4.boolean.opBoolean","COPY",FACE,{"derivedFrom":makeQuery(id+"F4.opExtrude","CAP_FACE",FACE,{"disambiguationData":[OSD([sQuery(id+"F3.wireOp",EDGE,"E33.2.4"),sQuery(id+"F3.wireOp",EDGE,"E33.2.5"),sQuery(id+"F3.wireOp",EDGE,"E33.2.6"),sQuery(id+"F3.wireOp",EDGE,"E33.2.7")])],"isStart":false})}),makeQuery(id+"F6.opRevolve","SWEPT_FACE",FACE,{"disambiguationData":[OSD([sQuery(id+"F5.wireOp",EDGE,"E35")])]})]});
            var Q39;
            Q39=makeQuery(id+"F6.boolean.opBoolean","INTERSECT",EDGE,{"derivedFrom":[makeQuery(id+"F4.boolean.opBoolean","COPY",FACE,{"derivedFrom":makeQuery(id+"F4.opExtrude","SWEPT_FACE",FACE,{"disambiguationData":[OSD([sQuery(id+"F3.wireOp",EDGE,"E33.2.6")])]})}),makeQuery(id+"F6.opRevolve","SWEPT_FACE",FACE,{"disambiguationData":[OSD([sQuery(id+"F5.wireOp",EDGE,"E35")])]})]});
            var Q40;
            Q40=makeQuery(id+"F6.boolean.opBoolean","INTERSECT",EDGE,{"disambiguationData":[OD(1.0)],"derivedFrom":[makeQuery(id+"F4.boolean.opBoolean","COPY",FACE,{"derivedFrom":makeQuery(id+"F4.opExtrude","SWEPT_FACE",FACE,{"disambiguationData":[OSD([sQuery(id+"F3.wireOp",EDGE,"E33.3.4")])]})}),makeQuery(id+"F6.opRevolve","SWEPT_FACE",FACE,{"disambiguationData":[OSD([sQuery(id+"F5.wireOp",EDGE,"E36")])]})]});
            var Q41;
            Q41=makeQuery(id+"F4.boolean.opBoolean","COPY",EDGE,{"derivedFrom":makeQuery(id+"F4.opExtrude","CAP_EDGE",EDGE,{"disambiguationData":[OSD([sQuery(id+"F3.wireOp",EDGE,"E33.3.4")])],"isStart":false})});
            var Q42;
            Q42=makeQuery(id+"F6.boolean.opBoolean","INTERSECT",EDGE,{"disambiguationData":[OD(0.0)],"derivedFrom":[makeQuery(id+"F4.boolean.opBoolean","COPY",FACE,{"derivedFrom":makeQuery(id+"F4.opExtrude","SWEPT_FACE",FACE,{"disambiguationData":[OSD([sQuery(id+"F3.wireOp",EDGE,"E33.3.4")])]})}),makeQuery(id+"F6.opRevolve","SWEPT_FACE",FACE,{"disambiguationData":[OSD([sQuery(id+"F5.wireOp",EDGE,"E36")])]})]});
            var Q43;
            Q43=makeQuery(id+"F6.boolean.opBoolean","INTERSECT",EDGE,{"derivedFrom":[makeQuery(id+"F4.boolean.opBoolean","COPY",FACE,{"derivedFrom":makeQuery(id+"F4.opExtrude","SWEPT_FACE",FACE,{"disambiguationData":[OSD([sQuery(id+"F3.wireOp",EDGE,"E33.3.5")])]})}),makeQuery(id+"F6.opRevolve","SWEPT_FACE",FACE,{"disambiguationData":[OSD([sQuery(id+"F5.wireOp",EDGE,"E36")])]})]});
            var Q44;
            Q44=makeQuery(id+"F6.boolean.opBoolean","INTERSECT",EDGE,{"derivedFrom":[makeQuery(id+"F4.boolean.opBoolean","COPY",FACE,{"derivedFrom":makeQuery(id+"F4.opExtrude","SWEPT_FACE",FACE,{"disambiguationData":[OSD([sQuery(id+"F3.wireOp",EDGE,"E33.3.5")])]})}),makeQuery(id+"F6.opRevolve","SWEPT_FACE",FACE,{"disambiguationData":[OSD([sQuery(id+"F5.wireOp",EDGE,"E34")])]})]});
            var Q45;
            Q45=makeQuery(id+"F6.boolean.opBoolean","INTERSECT",EDGE,{"derivedFrom":[makeQuery(id+"F4.boolean.opBoolean","COPY",FACE,{"derivedFrom":makeQuery(id+"F4.opExtrude","SWEPT_FACE",FACE,{"disambiguationData":[OSD([sQuery(id+"F3.wireOp",EDGE,"E33.3.6")])]})}),makeQuery(id+"F6.opRevolve","SWEPT_FACE",FACE,{"disambiguationData":[OSD([sQuery(id+"F5.wireOp",EDGE,"E36")])]})]});
            var Q46;
            Q46=makeQuery(id+"F6.boolean.opBoolean","INTERSECT",EDGE,{"derivedFrom":[makeQuery(id+"F4.boolean.opBoolean","COPY",FACE,{"derivedFrom":makeQuery(id+"F4.opExtrude","SWEPT_FACE",FACE,{"disambiguationData":[OSD([sQuery(id+"F3.wireOp",EDGE,"E33.3.6")])]})}),makeQuery(id+"F6.opRevolve","SWEPT_FACE",FACE,{"disambiguationData":[OSD([sQuery(id+"F5.wireOp",EDGE,"E34")])]})]});
            var Q47;
            Q47=makeQuery(id+"F6.boolean.opBoolean","INTERSECT",EDGE,{"derivedFrom":[makeQuery(id+"F4.boolean.opBoolean","COPY",FACE,{"derivedFrom":makeQuery(id+"F4.opExtrude","SWEPT_FACE",FACE,{"disambiguationData":[OSD([sQuery(id+"F3.wireOp",EDGE,"E33.3.6")])]})}),makeQuery(id+"F6.opRevolve","SWEPT_FACE",FACE,{"disambiguationData":[OSD([sQuery(id+"F5.wireOp",EDGE,"E35")])]})]});
            var Q48;
            Q48=makeQuery(id+"F6.boolean.opBoolean","INTERSECT",EDGE,{"derivedFrom":[makeQuery(id+"F4.boolean.opBoolean","COPY",FACE,{"derivedFrom":makeQuery(id+"F4.opExtrude","CAP_FACE",FACE,{"disambiguationData":[OSD([sQuery(id+"F3.wireOp",EDGE,"E33.3.4"),sQuery(id+"F3.wireOp",EDGE,"E33.3.5"),sQuery(id+"F3.wireOp",EDGE,"E33.3.6"),sQuery(id+"F3.wireOp",EDGE,"E33.3.7")])],"isStart":false})}),makeQuery(id+"F6.opRevolve","SWEPT_FACE",FACE,{"disambiguationData":[OSD([sQuery(id+"F5.wireOp",EDGE,"E35")])]})]});
            var Q49;
            Q49=makeQuery(id+"F6.boolean.opBoolean","INTERSECT",EDGE,{"derivedFrom":[makeQuery(id+"F4.boolean.opBoolean","COPY",FACE,{"derivedFrom":makeQuery(id+"F4.opExtrude","SWEPT_FACE",FACE,{"disambiguationData":[OSD([sQuery(id+"F3.wireOp",EDGE,"E33.3.5")])]})}),makeQuery(id+"F6.opRevolve","SWEPT_FACE",FACE,{"disambiguationData":[OSD([sQuery(id+"F5.wireOp",EDGE,"E35")])]})]});
            fillet(context, id + "F10", {"entities" : qUnion([Q0, Q1, Q2, Q3, Q4, Q5, Q6, Q7, Q8, Q9, Q10, Q11, Q12, Q13, Q14, Q15, Q16, Q17, Q18, Q19, Q20, Q21, Q22, Q23, Q24, Q25, Q26, Q27, Q28, Q29, Q30, Q31, Q32, Q33, Q34, Q35, Q36, Q37, Q38, Q39, Q40, Q41, Q42, Q43, Q44, Q45, Q46, Q47, Q48, Q49]), "radius" : 2.5 * mm, "tangentPropagation" : true, "allowEdgeOverflow" : false});
        }
        {
            var Q0;
            Q0=makeQuery(id+"F8.boolean.opBoolean","INTERSECT",EDGE,{"derivedFrom":[makeQuery(id+"F1.opRevolve","SWEPT_FACE",FACE,{"disambiguationData":[OSD([sQuery(id+"F0.wireOp",EDGE,"E10")])]}),makeQuery(id+"F8.opExtrude","SWEPT_FACE",FACE,{"disambiguationData":[OSD([sQuery(id+"F7.wireOp",EDGE,"E46.1.3")])]})]});
            var Q1;
            Q1=makeQuery(id+"F8.boolean.opBoolean","INTERSECT",EDGE,{"derivedFrom":[makeQuery(id+"F4.boolean.opBoolean","SPLIT",FACE,{"disambiguationData":[TD([makeQuery(id+"F4.opExtrude","SWEPT_FACE",FACE,{"disambiguationData":[OSD([sQuery(id+"F3.wireOp",EDGE,"E29")])]})])],"derivedFrom":makeQuery(id+"F1.opRevolve","SWEPT_FACE",FACE,{"disambiguationData":[OSD([sQuery(id+"F0.wireOp",EDGE,"E9")])]})}),makeQuery(id+"F8.opExtrude","SWEPT_FACE",FACE,{"disambiguationData":[OSD([sQuery(id+"F7.wireOp",EDGE,"E46.1.2")])]})]});
            var Q2;
            Q2=makeQuery(id+"F8.boolean.opBoolean","INTERSECT",EDGE,{"disambiguationData":[OD(0.0)],"derivedFrom":[makeQuery(id+"F4.boolean.opBoolean","SPLIT",FACE,{"disambiguationData":[TD([makeQuery(id+"F4.opExtrude","SWEPT_FACE",FACE,{"disambiguationData":[OSD([sQuery(id+"F3.wireOp",EDGE,"E29")])]})])],"derivedFrom":makeQuery(id+"F1.opRevolve","SWEPT_FACE",FACE,{"disambiguationData":[OSD([sQuery(id+"F0.wireOp",EDGE,"E9")])]})}),makeQuery(id+"F8.opExtrude","SWEPT_FACE",FACE,{"disambiguationData":[OSD([sQuery(id+"F7.wireOp",EDGE,"E46.1.3")])]})]});
            var Q3;
            Q3=makeQuery(id+"F8.boolean.opBoolean","INTERSECT",EDGE,{"derivedFrom":[makeQuery(id+"F4.boolean.opBoolean","SPLIT",FACE,{"disambiguationData":[TD([makeQuery(id+"F4.opExtrude","SWEPT_FACE",FACE,{"disambiguationData":[OSD([sQuery(id+"F3.wireOp",EDGE,"E29")])]})])],"derivedFrom":makeQuery(id+"F1.opRevolve","SWEPT_FACE",FACE,{"disambiguationData":[OSD([sQuery(id+"F0.wireOp",EDGE,"E9")])]})}),makeQuery(id+"F8.opExtrude","SWEPT_FACE",FACE,{"disambiguationData":[OSD([sQuery(id+"F7.wireOp",EDGE,"E46.1.1")])]})]});
            var Q4;
            Q4=makeQuery(id+"F8.boolean.opBoolean","INTERSECT",EDGE,{"derivedFrom":[makeQuery(id+"F1.opRevolve","SWEPT_FACE",FACE,{"disambiguationData":[OSD([sQuery(id+"F0.wireOp",EDGE,"E8")])]}),makeQuery(id+"F8.opExtrude","SWEPT_FACE",FACE,{"disambiguationData":[OSD([sQuery(id+"F7.wireOp",EDGE,"E46.1.1")])]})]});
            var Q5;
            Q5=makeQuery(id+"F8.boolean.opBoolean","INTERSECT",EDGE,{"disambiguationData":[OD(1.0)],"derivedFrom":[makeQuery(id+"F4.boolean.opBoolean","SPLIT",FACE,{"disambiguationData":[TD([makeQuery(id+"F4.opExtrude","SWEPT_FACE",FACE,{"disambiguationData":[OSD([sQuery(id+"F3.wireOp",EDGE,"E29")])]})])],"derivedFrom":makeQuery(id+"F1.opRevolve","SWEPT_FACE",FACE,{"disambiguationData":[OSD([sQuery(id+"F0.wireOp",EDGE,"E9")])]})}),makeQuery(id+"F8.opExtrude","SWEPT_FACE",FACE,{"disambiguationData":[OSD([sQuery(id+"F7.wireOp",EDGE,"E46.1.3")])]})]});
            var Q6;
            Q6=makeQuery(id+"F8.boolean.opBoolean","INTERSECT",EDGE,{"derivedFrom":[makeQuery(id+"F4.boolean.opBoolean","SPLIT",FACE,{"disambiguationData":[TD([makeQuery(id+"F4.opExtrude","SWEPT_FACE",FACE,{"disambiguationData":[OSD([sQuery(id+"F3.wireOp",EDGE,"E29")])]})])],"derivedFrom":makeQuery(id+"F1.opRevolve","SWEPT_FACE",FACE,{"disambiguationData":[OSD([sQuery(id+"F0.wireOp",EDGE,"E9")])]})}),makeQuery(id+"F8.opExtrude","SWEPT_FACE",FACE,{"disambiguationData":[OSD([sQuery(id+"F7.wireOp",EDGE,"E46.1.4")])]})]});
            var Q7;
            Q7=makeQuery(id+"F8.boolean.opBoolean","INTERSECT",EDGE,{"derivedFrom":[makeQuery(id+"F4.boolean.opBoolean","SPLIT",FACE,{"disambiguationData":[TD([makeQuery(id+"F4.opExtrude","SWEPT_FACE",FACE,{"disambiguationData":[OSD([sQuery(id+"F3.wireOp",EDGE,"E29")])]})])],"derivedFrom":makeQuery(id+"F1.opRevolve","SWEPT_FACE",FACE,{"disambiguationData":[OSD([sQuery(id+"F0.wireOp",EDGE,"E9")])]})}),makeQuery(id+"F8.opExtrude","SWEPT_FACE",FACE,{"disambiguationData":[OSD([sQuery(id+"F7.wireOp",EDGE,"E46.1.5")])]})]});
            var Q8;
            Q8=makeQuery(id+"F8.boolean.opBoolean","INTERSECT",EDGE,{"derivedFrom":[makeQuery(id+"F1.opRevolve","SWEPT_FACE",FACE,{"disambiguationData":[OSD([sQuery(id+"F0.wireOp",EDGE,"E8")])]}),makeQuery(id+"F8.opExtrude","SWEPT_FACE",FACE,{"disambiguationData":[OSD([sQuery(id+"F7.wireOp",EDGE,"E46.1.5")])]})]});
            var Q9;
            Q9=makeQuery(id+"F8.boolean.opBoolean","INTERSECT",EDGE,{"derivedFrom":[makeQuery(id+"F1.opRevolve","SWEPT_FACE",FACE,{"disambiguationData":[OSD([sQuery(id+"F0.wireOp",EDGE,"E8")])]}),makeQuery(id+"F8.opExtrude","SWEPT_FACE",FACE,{"disambiguationData":[OSD([sQuery(id+"F7.wireOp",EDGE,"E46.1.0")])]})]});
            var Q10;
            Q10=makeQuery(id+"F8.boolean.opBoolean","INTERSECT",EDGE,{"derivedFrom":[makeQuery(id+"F4.boolean.opBoolean","SPLIT",FACE,{"disambiguationData":[TD([makeQuery(id+"F4.opExtrude","SWEPT_FACE",FACE,{"disambiguationData":[OSD([sQuery(id+"F3.wireOp",EDGE,"E33.1.0")])]})])],"derivedFrom":makeQuery(id+"F1.opRevolve","SWEPT_FACE",FACE,{"disambiguationData":[OSD([sQuery(id+"F0.wireOp",EDGE,"E9")])]})}),makeQuery(id+"F8.opExtrude","SWEPT_FACE",FACE,{"disambiguationData":[OSD([sQuery(id+"F7.wireOp",EDGE,"E46.2.2")])]})]});
            var Q11;
            Q11=makeQuery(id+"F8.boolean.opBoolean","INTERSECT",EDGE,{"derivedFrom":[makeQuery(id+"F1.opRevolve","SWEPT_FACE",FACE,{"disambiguationData":[OSD([sQuery(id+"F0.wireOp",EDGE,"E10")])]}),makeQuery(id+"F8.opExtrude","SWEPT_FACE",FACE,{"disambiguationData":[OSD([sQuery(id+"F7.wireOp",EDGE,"E46.2.3")])]})]});
            var Q12;
            Q12=makeQuery(id+"F8.boolean.opBoolean","INTERSECT",EDGE,{"derivedFrom":[makeQuery(id+"F4.boolean.opBoolean","SPLIT",FACE,{"disambiguationData":[TD([makeQuery(id+"F4.opExtrude","SWEPT_FACE",FACE,{"disambiguationData":[OSD([sQuery(id+"F3.wireOp",EDGE,"E33.1.0")])]})])],"derivedFrom":makeQuery(id+"F1.opRevolve","SWEPT_FACE",FACE,{"disambiguationData":[OSD([sQuery(id+"F0.wireOp",EDGE,"E9")])]})}),makeQuery(id+"F8.opExtrude","SWEPT_FACE",FACE,{"disambiguationData":[OSD([sQuery(id+"F7.wireOp",EDGE,"E46.2.4")])]})]});
            var Q13;
            Q13=makeQuery(id+"F8.boolean.opBoolean","INTERSECT",EDGE,{"derivedFrom":[makeQuery(id+"F1.opRevolve","SWEPT_FACE",FACE,{"disambiguationData":[OSD([sQuery(id+"F0.wireOp",EDGE,"E8")])]}),makeQuery(id+"F8.opExtrude","SWEPT_FACE",FACE,{"disambiguationData":[OSD([sQuery(id+"F7.wireOp",EDGE,"E46.2.0")])]})]});
            var Q14;
            Q14=makeQuery(id+"F8.boolean.opBoolean","INTERSECT",EDGE,{"derivedFrom":[makeQuery(id+"F1.opRevolve","SWEPT_FACE",FACE,{"disambiguationData":[OSD([sQuery(id+"F0.wireOp",EDGE,"E8")])]}),makeQuery(id+"F8.opExtrude","SWEPT_FACE",FACE,{"disambiguationData":[OSD([sQuery(id+"F7.wireOp",EDGE,"E46.2.1")])]})]});
            var Q15;
            Q15=makeQuery(id+"F8.boolean.opBoolean","INTERSECT",EDGE,{"derivedFrom":[makeQuery(id+"F4.boolean.opBoolean","SPLIT",FACE,{"disambiguationData":[TD([makeQuery(id+"F4.opExtrude","SWEPT_FACE",FACE,{"disambiguationData":[OSD([sQuery(id+"F3.wireOp",EDGE,"E33.1.0")])]})])],"derivedFrom":makeQuery(id+"F1.opRevolve","SWEPT_FACE",FACE,{"disambiguationData":[OSD([sQuery(id+"F0.wireOp",EDGE,"E9")])]})}),makeQuery(id+"F8.opExtrude","SWEPT_FACE",FACE,{"disambiguationData":[OSD([sQuery(id+"F7.wireOp",EDGE,"E46.2.1")])]})]});
            var Q16;
            Q16=makeQuery(id+"F8.boolean.opBoolean","INTERSECT",EDGE,{"derivedFrom":[makeQuery(id+"F1.opRevolve","SWEPT_FACE",FACE,{"disambiguationData":[OSD([sQuery(id+"F0.wireOp",EDGE,"E8")])]}),makeQuery(id+"F8.opExtrude","SWEPT_FACE",FACE,{"disambiguationData":[OSD([sQuery(id+"F7.wireOp",EDGE,"E46.2.5")])]})]});
            var Q17;
            Q17=makeQuery(id+"F8.boolean.opBoolean","INTERSECT",EDGE,{"derivedFrom":[makeQuery(id+"F4.boolean.opBoolean","SPLIT",FACE,{"disambiguationData":[TD([makeQuery(id+"F4.opExtrude","SWEPT_FACE",FACE,{"disambiguationData":[OSD([sQuery(id+"F3.wireOp",EDGE,"E33.1.0")])]})])],"derivedFrom":makeQuery(id+"F1.opRevolve","SWEPT_FACE",FACE,{"disambiguationData":[OSD([sQuery(id+"F0.wireOp",EDGE,"E9")])]})}),makeQuery(id+"F8.opExtrude","SWEPT_FACE",FACE,{"disambiguationData":[OSD([sQuery(id+"F7.wireOp",EDGE,"E46.2.5")])]})]});
            var Q18;
            Q18=makeQuery(id+"F8.boolean.opBoolean","INTERSECT",EDGE,{"disambiguationData":[OD(1.0)],"derivedFrom":[makeQuery(id+"F4.boolean.opBoolean","SPLIT",FACE,{"disambiguationData":[TD([makeQuery(id+"F4.opExtrude","SWEPT_FACE",FACE,{"disambiguationData":[OSD([sQuery(id+"F3.wireOp",EDGE,"E33.1.0")])]})])],"derivedFrom":makeQuery(id+"F1.opRevolve","SWEPT_FACE",FACE,{"disambiguationData":[OSD([sQuery(id+"F0.wireOp",EDGE,"E9")])]})}),makeQuery(id+"F8.opExtrude","SWEPT_FACE",FACE,{"disambiguationData":[OSD([sQuery(id+"F7.wireOp",EDGE,"E46.2.3")])]})]});
            var Q19;
            Q19=makeQuery(id+"F8.boolean.opBoolean","INTERSECT",EDGE,{"disambiguationData":[OD(0.0)],"derivedFrom":[makeQuery(id+"F4.boolean.opBoolean","SPLIT",FACE,{"disambiguationData":[TD([makeQuery(id+"F4.opExtrude","SWEPT_FACE",FACE,{"disambiguationData":[OSD([sQuery(id+"F3.wireOp",EDGE,"E33.1.0")])]})])],"derivedFrom":makeQuery(id+"F1.opRevolve","SWEPT_FACE",FACE,{"disambiguationData":[OSD([sQuery(id+"F0.wireOp",EDGE,"E9")])]})}),makeQuery(id+"F8.opExtrude","SWEPT_FACE",FACE,{"disambiguationData":[OSD([sQuery(id+"F7.wireOp",EDGE,"E46.2.3")])]})]});
            var Q20;
            Q20=makeQuery(id+"F8.boolean.opBoolean","INTERSECT",EDGE,{"derivedFrom":[makeQuery(id+"F1.opRevolve","SWEPT_FACE",FACE,{"disambiguationData":[OSD([sQuery(id+"F0.wireOp",EDGE,"E8")])]}),makeQuery(id+"F8.opExtrude","SWEPT_FACE",FACE,{"disambiguationData":[OSD([sQuery(id+"F7.wireOp",EDGE,"E46.3.1")])]})]});
            var Q21;
            Q21=makeQuery(id+"F8.boolean.opBoolean","INTERSECT",EDGE,{"derivedFrom":[makeQuery(id+"F4.boolean.opBoolean","SPLIT",FACE,{"disambiguationData":[TD([makeQuery(id+"F4.opExtrude","SWEPT_FACE",FACE,{"disambiguationData":[OSD([sQuery(id+"F3.wireOp",EDGE,"E33.1.5")])]})])],"derivedFrom":makeQuery(id+"F1.opRevolve","SWEPT_FACE",FACE,{"disambiguationData":[OSD([sQuery(id+"F0.wireOp",EDGE,"E9")])]})}),makeQuery(id+"F8.opExtrude","SWEPT_FACE",FACE,{"disambiguationData":[OSD([sQuery(id+"F7.wireOp",EDGE,"E46.3.1")])]})]});
            var Q22;
            Q22=makeQuery(id+"F8.boolean.opBoolean","INTERSECT",EDGE,{"derivedFrom":[makeQuery(id+"F4.boolean.opBoolean","SPLIT",FACE,{"disambiguationData":[TD([makeQuery(id+"F4.opExtrude","SWEPT_FACE",FACE,{"disambiguationData":[OSD([sQuery(id+"F3.wireOp",EDGE,"E33.1.5")])]})])],"derivedFrom":makeQuery(id+"F1.opRevolve","SWEPT_FACE",FACE,{"disambiguationData":[OSD([sQuery(id+"F0.wireOp",EDGE,"E9")])]})}),makeQuery(id+"F8.opExtrude","SWEPT_FACE",FACE,{"disambiguationData":[OSD([sQuery(id+"F7.wireOp",EDGE,"E46.3.2")])]})]});
            var Q23;
            Q23=makeQuery(id+"F8.boolean.opBoolean","INTERSECT",EDGE,{"disambiguationData":[OD(0.0)],"derivedFrom":[makeQuery(id+"F4.boolean.opBoolean","SPLIT",FACE,{"disambiguationData":[TD([makeQuery(id+"F4.opExtrude","SWEPT_FACE",FACE,{"disambiguationData":[OSD([sQuery(id+"F3.wireOp",EDGE,"E33.1.5")])]})])],"derivedFrom":makeQuery(id+"F1.opRevolve","SWEPT_FACE",FACE,{"disambiguationData":[OSD([sQuery(id+"F0.wireOp",EDGE,"E9")])]})}),makeQuery(id+"F8.opExtrude","SWEPT_FACE",FACE,{"disambiguationData":[OSD([sQuery(id+"F7.wireOp",EDGE,"E46.3.3")])]})]});
            var Q24;
            Q24=makeQuery(id+"F8.boolean.opBoolean","INTERSECT",EDGE,{"derivedFrom":[makeQuery(id+"F1.opRevolve","SWEPT_FACE",FACE,{"disambiguationData":[OSD([sQuery(id+"F0.wireOp",EDGE,"E10")])]}),makeQuery(id+"F8.opExtrude","SWEPT_FACE",FACE,{"disambiguationData":[OSD([sQuery(id+"F7.wireOp",EDGE,"E46.3.3")])]})]});
            var Q25;
            Q25=makeQuery(id+"F8.boolean.opBoolean","INTERSECT",EDGE,{"disambiguationData":[OD(1.0)],"derivedFrom":[makeQuery(id+"F4.boolean.opBoolean","SPLIT",FACE,{"disambiguationData":[TD([makeQuery(id+"F4.opExtrude","SWEPT_FACE",FACE,{"disambiguationData":[OSD([sQuery(id+"F3.wireOp",EDGE,"E33.1.5")])]})])],"derivedFrom":makeQuery(id+"F1.opRevolve","SWEPT_FACE",FACE,{"disambiguationData":[OSD([sQuery(id+"F0.wireOp",EDGE,"E9")])]})}),makeQuery(id+"F8.opExtrude","SWEPT_FACE",FACE,{"disambiguationData":[OSD([sQuery(id+"F7.wireOp",EDGE,"E46.3.3")])]})]});
            var Q26;
            Q26=makeQuery(id+"F8.boolean.opBoolean","INTERSECT",EDGE,{"derivedFrom":[makeQuery(id+"F4.boolean.opBoolean","SPLIT",FACE,{"disambiguationData":[TD([makeQuery(id+"F4.opExtrude","SWEPT_FACE",FACE,{"disambiguationData":[OSD([sQuery(id+"F3.wireOp",EDGE,"E33.1.5")])]})])],"derivedFrom":makeQuery(id+"F1.opRevolve","SWEPT_FACE",FACE,{"disambiguationData":[OSD([sQuery(id+"F0.wireOp",EDGE,"E9")])]})}),makeQuery(id+"F8.opExtrude","SWEPT_FACE",FACE,{"disambiguationData":[OSD([sQuery(id+"F7.wireOp",EDGE,"E46.3.4")])]})]});
            var Q27;
            Q27=makeQuery(id+"F8.boolean.opBoolean","INTERSECT",EDGE,{"derivedFrom":[makeQuery(id+"F4.boolean.opBoolean","SPLIT",FACE,{"disambiguationData":[TD([makeQuery(id+"F4.opExtrude","SWEPT_FACE",FACE,{"disambiguationData":[OSD([sQuery(id+"F3.wireOp",EDGE,"E33.1.5")])]})])],"derivedFrom":makeQuery(id+"F1.opRevolve","SWEPT_FACE",FACE,{"disambiguationData":[OSD([sQuery(id+"F0.wireOp",EDGE,"E9")])]})}),makeQuery(id+"F8.opExtrude","SWEPT_FACE",FACE,{"disambiguationData":[OSD([sQuery(id+"F7.wireOp",EDGE,"E46.3.5")])]})]});
            var Q28;
            Q28=makeQuery(id+"F8.boolean.opBoolean","INTERSECT",EDGE,{"derivedFrom":[makeQuery(id+"F1.opRevolve","SWEPT_FACE",FACE,{"disambiguationData":[OSD([sQuery(id+"F0.wireOp",EDGE,"E8")])]}),makeQuery(id+"F8.opExtrude","SWEPT_FACE",FACE,{"disambiguationData":[OSD([sQuery(id+"F7.wireOp",EDGE,"E46.3.5")])]})]});
            var Q29;
            Q29=makeQuery(id+"F8.boolean.opBoolean","INTERSECT",EDGE,{"derivedFrom":[makeQuery(id+"F1.opRevolve","SWEPT_FACE",FACE,{"disambiguationData":[OSD([sQuery(id+"F0.wireOp",EDGE,"E8")])]}),makeQuery(id+"F8.opExtrude","SWEPT_FACE",FACE,{"disambiguationData":[OSD([sQuery(id+"F7.wireOp",EDGE,"E46.3.0")])]})]});
            var Q30;
            Q30=makeQuery(id+"F8.boolean.opBoolean","INTERSECT",EDGE,{"derivedFrom":[makeQuery(id+"F4.boolean.opBoolean","SPLIT",FACE,{"disambiguationData":[TD([makeQuery(id+"F4.opExtrude","SWEPT_FACE",FACE,{"disambiguationData":[OSD([sQuery(id+"F3.wireOp",EDGE,"E33.2.0")])]})])],"derivedFrom":makeQuery(id+"F1.opRevolve","SWEPT_FACE",FACE,{"disambiguationData":[OSD([sQuery(id+"F0.wireOp",EDGE,"E9")])]})}),makeQuery(id+"F8.opExtrude","SWEPT_FACE",FACE,{"disambiguationData":[OSD([sQuery(id+"F7.wireOp",EDGE,"E46.4.2")])]})]});
            var Q31;
            Q31=makeQuery(id+"F8.boolean.opBoolean","INTERSECT",EDGE,{"disambiguationData":[OD(0.0)],"derivedFrom":[makeQuery(id+"F4.boolean.opBoolean","SPLIT",FACE,{"disambiguationData":[TD([makeQuery(id+"F4.opExtrude","SWEPT_FACE",FACE,{"disambiguationData":[OSD([sQuery(id+"F3.wireOp",EDGE,"E33.2.0")])]})])],"derivedFrom":makeQuery(id+"F1.opRevolve","SWEPT_FACE",FACE,{"disambiguationData":[OSD([sQuery(id+"F0.wireOp",EDGE,"E9")])]})}),makeQuery(id+"F8.opExtrude","SWEPT_FACE",FACE,{"disambiguationData":[OSD([sQuery(id+"F7.wireOp",EDGE,"E46.4.3")])]})]});
            var Q32;
            Q32=makeQuery(id+"F8.boolean.opBoolean","INTERSECT",EDGE,{"derivedFrom":[makeQuery(id+"F1.opRevolve","SWEPT_FACE",FACE,{"disambiguationData":[OSD([sQuery(id+"F0.wireOp",EDGE,"E10")])]}),makeQuery(id+"F8.opExtrude","SWEPT_FACE",FACE,{"disambiguationData":[OSD([sQuery(id+"F7.wireOp",EDGE,"E46.4.3")])]})]});
            var Q33;
            Q33=makeQuery(id+"F8.boolean.opBoolean","INTERSECT",EDGE,{"disambiguationData":[OD(1.0)],"derivedFrom":[makeQuery(id+"F4.boolean.opBoolean","SPLIT",FACE,{"disambiguationData":[TD([makeQuery(id+"F4.opExtrude","SWEPT_FACE",FACE,{"disambiguationData":[OSD([sQuery(id+"F3.wireOp",EDGE,"E33.2.0")])]})])],"derivedFrom":makeQuery(id+"F1.opRevolve","SWEPT_FACE",FACE,{"disambiguationData":[OSD([sQuery(id+"F0.wireOp",EDGE,"E9")])]})}),makeQuery(id+"F8.opExtrude","SWEPT_FACE",FACE,{"disambiguationData":[OSD([sQuery(id+"F7.wireOp",EDGE,"E46.4.3")])]})]});
            var Q34;
            Q34=makeQuery(id+"F8.boolean.opBoolean","INTERSECT",EDGE,{"derivedFrom":[makeQuery(id+"F4.boolean.opBoolean","SPLIT",FACE,{"disambiguationData":[TD([makeQuery(id+"F4.opExtrude","SWEPT_FACE",FACE,{"disambiguationData":[OSD([sQuery(id+"F3.wireOp",EDGE,"E33.2.0")])]})])],"derivedFrom":makeQuery(id+"F1.opRevolve","SWEPT_FACE",FACE,{"disambiguationData":[OSD([sQuery(id+"F0.wireOp",EDGE,"E9")])]})}),makeQuery(id+"F8.opExtrude","SWEPT_FACE",FACE,{"disambiguationData":[OSD([sQuery(id+"F7.wireOp",EDGE,"E46.4.4")])]})]});
            var Q35;
            Q35=makeQuery(id+"F8.boolean.opBoolean","INTERSECT",EDGE,{"derivedFrom":[makeQuery(id+"F4.boolean.opBoolean","SPLIT",FACE,{"disambiguationData":[TD([makeQuery(id+"F4.opExtrude","SWEPT_FACE",FACE,{"disambiguationData":[OSD([sQuery(id+"F3.wireOp",EDGE,"E33.2.0")])]})])],"derivedFrom":makeQuery(id+"F1.opRevolve","SWEPT_FACE",FACE,{"disambiguationData":[OSD([sQuery(id+"F0.wireOp",EDGE,"E9")])]})}),makeQuery(id+"F8.opExtrude","SWEPT_FACE",FACE,{"disambiguationData":[OSD([sQuery(id+"F7.wireOp",EDGE,"E46.4.5")])]})]});
            var Q36;
            Q36=makeQuery(id+"F8.boolean.opBoolean","INTERSECT",EDGE,{"derivedFrom":[makeQuery(id+"F1.opRevolve","SWEPT_FACE",FACE,{"disambiguationData":[OSD([sQuery(id+"F0.wireOp",EDGE,"E8")])]}),makeQuery(id+"F8.opExtrude","SWEPT_FACE",FACE,{"disambiguationData":[OSD([sQuery(id+"F7.wireOp",EDGE,"E46.4.5")])]})]});
            var Q37;
            Q37=makeQuery(id+"F8.boolean.opBoolean","INTERSECT",EDGE,{"derivedFrom":[makeQuery(id+"F1.opRevolve","SWEPT_FACE",FACE,{"disambiguationData":[OSD([sQuery(id+"F0.wireOp",EDGE,"E8")])]}),makeQuery(id+"F8.opExtrude","SWEPT_FACE",FACE,{"disambiguationData":[OSD([sQuery(id+"F7.wireOp",EDGE,"E46.4.0")])]})]});
            var Q38;
            Q38=makeQuery(id+"F8.boolean.opBoolean","INTERSECT",EDGE,{"derivedFrom":[makeQuery(id+"F4.boolean.opBoolean","SPLIT",FACE,{"disambiguationData":[TD([makeQuery(id+"F4.opExtrude","SWEPT_FACE",FACE,{"disambiguationData":[OSD([sQuery(id+"F3.wireOp",EDGE,"E33.2.0")])]})])],"derivedFrom":makeQuery(id+"F1.opRevolve","SWEPT_FACE",FACE,{"disambiguationData":[OSD([sQuery(id+"F0.wireOp",EDGE,"E9")])]})}),makeQuery(id+"F8.opExtrude","SWEPT_FACE",FACE,{"disambiguationData":[OSD([sQuery(id+"F7.wireOp",EDGE,"E46.4.1")])]})]});
            var Q39;
            Q39=makeQuery(id+"F8.boolean.opBoolean","INTERSECT",EDGE,{"derivedFrom":[makeQuery(id+"F1.opRevolve","SWEPT_FACE",FACE,{"disambiguationData":[OSD([sQuery(id+"F0.wireOp",EDGE,"E8")])]}),makeQuery(id+"F8.opExtrude","SWEPT_FACE",FACE,{"disambiguationData":[OSD([sQuery(id+"F7.wireOp",EDGE,"E46.4.1")])]})]});
            var Q40;
            Q40=makeQuery(id+"F8.boolean.opBoolean","INTERSECT",EDGE,{"disambiguationData":[OD(0.0)],"derivedFrom":[makeQuery(id+"F4.boolean.opBoolean","SPLIT",FACE,{"disambiguationData":[TD([makeQuery(id+"F4.opExtrude","SWEPT_FACE",FACE,{"disambiguationData":[OSD([sQuery(id+"F3.wireOp",EDGE,"E33.2.5")])]})])],"derivedFrom":makeQuery(id+"F1.opRevolve","SWEPT_FACE",FACE,{"disambiguationData":[OSD([sQuery(id+"F0.wireOp",EDGE,"E9")])]})}),makeQuery(id+"F8.opExtrude","SWEPT_FACE",FACE,{"disambiguationData":[OSD([sQuery(id+"F7.wireOp",EDGE,"E46.5.3")])]})]});
            var Q41;
            Q41=makeQuery(id+"F8.boolean.opBoolean","INTERSECT",EDGE,{"derivedFrom":[makeQuery(id+"F1.opRevolve","SWEPT_FACE",FACE,{"disambiguationData":[OSD([sQuery(id+"F0.wireOp",EDGE,"E10")])]}),makeQuery(id+"F8.opExtrude","SWEPT_FACE",FACE,{"disambiguationData":[OSD([sQuery(id+"F7.wireOp",EDGE,"E46.5.3")])]})]});
            var Q42;
            Q42=makeQuery(id+"F8.boolean.opBoolean","INTERSECT",EDGE,{"derivedFrom":[makeQuery(id+"F4.boolean.opBoolean","SPLIT",FACE,{"disambiguationData":[TD([makeQuery(id+"F4.opExtrude","SWEPT_FACE",FACE,{"disambiguationData":[OSD([sQuery(id+"F3.wireOp",EDGE,"E33.2.5")])]})])],"derivedFrom":makeQuery(id+"F1.opRevolve","SWEPT_FACE",FACE,{"disambiguationData":[OSD([sQuery(id+"F0.wireOp",EDGE,"E9")])]})}),makeQuery(id+"F8.opExtrude","SWEPT_FACE",FACE,{"disambiguationData":[OSD([sQuery(id+"F7.wireOp",EDGE,"E46.5.2")])]})]});
            var Q43;
            Q43=makeQuery(id+"F8.boolean.opBoolean","INTERSECT",EDGE,{"derivedFrom":[makeQuery(id+"F4.boolean.opBoolean","SPLIT",FACE,{"disambiguationData":[TD([makeQuery(id+"F4.opExtrude","SWEPT_FACE",FACE,{"disambiguationData":[OSD([sQuery(id+"F3.wireOp",EDGE,"E33.2.5")])]})])],"derivedFrom":makeQuery(id+"F1.opRevolve","SWEPT_FACE",FACE,{"disambiguationData":[OSD([sQuery(id+"F0.wireOp",EDGE,"E9")])]})}),makeQuery(id+"F8.opExtrude","SWEPT_FACE",FACE,{"disambiguationData":[OSD([sQuery(id+"F7.wireOp",EDGE,"E46.5.1")])]})]});
            var Q44;
            Q44=makeQuery(id+"F8.boolean.opBoolean","INTERSECT",EDGE,{"derivedFrom":[makeQuery(id+"F1.opRevolve","SWEPT_FACE",FACE,{"disambiguationData":[OSD([sQuery(id+"F0.wireOp",EDGE,"E8")])]}),makeQuery(id+"F8.opExtrude","SWEPT_FACE",FACE,{"disambiguationData":[OSD([sQuery(id+"F7.wireOp",EDGE,"E46.5.1")])]})]});
            var Q45;
            Q45=makeQuery(id+"F8.boolean.opBoolean","INTERSECT",EDGE,{"disambiguationData":[OD(1.0)],"derivedFrom":[makeQuery(id+"F4.boolean.opBoolean","SPLIT",FACE,{"disambiguationData":[TD([makeQuery(id+"F4.opExtrude","SWEPT_FACE",FACE,{"disambiguationData":[OSD([sQuery(id+"F3.wireOp",EDGE,"E33.2.5")])]})])],"derivedFrom":makeQuery(id+"F1.opRevolve","SWEPT_FACE",FACE,{"disambiguationData":[OSD([sQuery(id+"F0.wireOp",EDGE,"E9")])]})}),makeQuery(id+"F8.opExtrude","SWEPT_FACE",FACE,{"disambiguationData":[OSD([sQuery(id+"F7.wireOp",EDGE,"E46.5.3")])]})]});
            var Q46;
            Q46=makeQuery(id+"F8.boolean.opBoolean","INTERSECT",EDGE,{"derivedFrom":[makeQuery(id+"F4.boolean.opBoolean","SPLIT",FACE,{"disambiguationData":[TD([makeQuery(id+"F4.opExtrude","SWEPT_FACE",FACE,{"disambiguationData":[OSD([sQuery(id+"F3.wireOp",EDGE,"E33.2.5")])]})])],"derivedFrom":makeQuery(id+"F1.opRevolve","SWEPT_FACE",FACE,{"disambiguationData":[OSD([sQuery(id+"F0.wireOp",EDGE,"E9")])]})}),makeQuery(id+"F8.opExtrude","SWEPT_FACE",FACE,{"disambiguationData":[OSD([sQuery(id+"F7.wireOp",EDGE,"E46.5.4")])]})]});
            var Q47;
            Q47=makeQuery(id+"F8.boolean.opBoolean","INTERSECT",EDGE,{"derivedFrom":[makeQuery(id+"F4.boolean.opBoolean","SPLIT",FACE,{"disambiguationData":[TD([makeQuery(id+"F4.opExtrude","SWEPT_FACE",FACE,{"disambiguationData":[OSD([sQuery(id+"F3.wireOp",EDGE,"E33.2.5")])]})])],"derivedFrom":makeQuery(id+"F1.opRevolve","SWEPT_FACE",FACE,{"disambiguationData":[OSD([sQuery(id+"F0.wireOp",EDGE,"E9")])]})}),makeQuery(id+"F8.opExtrude","SWEPT_FACE",FACE,{"disambiguationData":[OSD([sQuery(id+"F7.wireOp",EDGE,"E46.5.5")])]})]});
            var Q48;
            Q48=makeQuery(id+"F8.boolean.opBoolean","INTERSECT",EDGE,{"derivedFrom":[makeQuery(id+"F1.opRevolve","SWEPT_FACE",FACE,{"disambiguationData":[OSD([sQuery(id+"F0.wireOp",EDGE,"E8")])]}),makeQuery(id+"F8.opExtrude","SWEPT_FACE",FACE,{"disambiguationData":[OSD([sQuery(id+"F7.wireOp",EDGE,"E46.5.5")])]})]});
            var Q49;
            Q49=makeQuery(id+"F8.boolean.opBoolean","INTERSECT",EDGE,{"derivedFrom":[makeQuery(id+"F1.opRevolve","SWEPT_FACE",FACE,{"disambiguationData":[OSD([sQuery(id+"F0.wireOp",EDGE,"E8")])]}),makeQuery(id+"F8.opExtrude","SWEPT_FACE",FACE,{"disambiguationData":[OSD([sQuery(id+"F7.wireOp",EDGE,"E46.5.0")])]})]});
            var Q50;
            Q50=makeQuery(id+"F8.boolean.opBoolean","INTERSECT",EDGE,{"derivedFrom":[makeQuery(id+"F1.opRevolve","SWEPT_FACE",FACE,{"disambiguationData":[OSD([sQuery(id+"F0.wireOp",EDGE,"E10")])]}),makeQuery(id+"F8.opExtrude","SWEPT_FACE",FACE,{"disambiguationData":[OSD([sQuery(id+"F7.wireOp",EDGE,"E46.6.3")])]})]});
            var Q51;
            Q51=makeQuery(id+"F8.boolean.opBoolean","INTERSECT",EDGE,{"disambiguationData":[OD(1.0)],"derivedFrom":[makeQuery(id+"F4.boolean.opBoolean","SPLIT",FACE,{"disambiguationData":[TD([makeQuery(id+"F4.opExtrude","SWEPT_FACE",FACE,{"disambiguationData":[OSD([sQuery(id+"F3.wireOp",EDGE,"E33.3.0")])]})])],"derivedFrom":makeQuery(id+"F1.opRevolve","SWEPT_FACE",FACE,{"disambiguationData":[OSD([sQuery(id+"F0.wireOp",EDGE,"E9")])]})}),makeQuery(id+"F8.opExtrude","SWEPT_FACE",FACE,{"disambiguationData":[OSD([sQuery(id+"F7.wireOp",EDGE,"E46.6.3")])]})]});
            var Q52;
            Q52=makeQuery(id+"F8.boolean.opBoolean","INTERSECT",EDGE,{"derivedFrom":[makeQuery(id+"F4.boolean.opBoolean","SPLIT",FACE,{"disambiguationData":[TD([makeQuery(id+"F4.opExtrude","SWEPT_FACE",FACE,{"disambiguationData":[OSD([sQuery(id+"F3.wireOp",EDGE,"E33.3.0")])]})])],"derivedFrom":makeQuery(id+"F1.opRevolve","SWEPT_FACE",FACE,{"disambiguationData":[OSD([sQuery(id+"F0.wireOp",EDGE,"E9")])]})}),makeQuery(id+"F8.opExtrude","SWEPT_FACE",FACE,{"disambiguationData":[OSD([sQuery(id+"F7.wireOp",EDGE,"E46.6.4")])]})]});
            var Q53;
            Q53=makeQuery(id+"F8.boolean.opBoolean","INTERSECT",EDGE,{"disambiguationData":[OD(0.0)],"derivedFrom":[makeQuery(id+"F4.boolean.opBoolean","SPLIT",FACE,{"disambiguationData":[TD([makeQuery(id+"F4.opExtrude","SWEPT_FACE",FACE,{"disambiguationData":[OSD([sQuery(id+"F3.wireOp",EDGE,"E33.3.0")])]})])],"derivedFrom":makeQuery(id+"F1.opRevolve","SWEPT_FACE",FACE,{"disambiguationData":[OSD([sQuery(id+"F0.wireOp",EDGE,"E9")])]})}),makeQuery(id+"F8.opExtrude","SWEPT_FACE",FACE,{"disambiguationData":[OSD([sQuery(id+"F7.wireOp",EDGE,"E46.6.3")])]})]});
            var Q54;
            Q54=makeQuery(id+"F8.boolean.opBoolean","INTERSECT",EDGE,{"derivedFrom":[makeQuery(id+"F4.boolean.opBoolean","SPLIT",FACE,{"disambiguationData":[TD([makeQuery(id+"F4.opExtrude","SWEPT_FACE",FACE,{"disambiguationData":[OSD([sQuery(id+"F3.wireOp",EDGE,"E33.3.0")])]})])],"derivedFrom":makeQuery(id+"F1.opRevolve","SWEPT_FACE",FACE,{"disambiguationData":[OSD([sQuery(id+"F0.wireOp",EDGE,"E9")])]})}),makeQuery(id+"F8.opExtrude","SWEPT_FACE",FACE,{"disambiguationData":[OSD([sQuery(id+"F7.wireOp",EDGE,"E46.6.2")])]})]});
            var Q55;
            Q55=makeQuery(id+"F8.boolean.opBoolean","INTERSECT",EDGE,{"derivedFrom":[makeQuery(id+"F4.boolean.opBoolean","SPLIT",FACE,{"disambiguationData":[TD([makeQuery(id+"F4.opExtrude","SWEPT_FACE",FACE,{"disambiguationData":[OSD([sQuery(id+"F3.wireOp",EDGE,"E33.3.0")])]})])],"derivedFrom":makeQuery(id+"F1.opRevolve","SWEPT_FACE",FACE,{"disambiguationData":[OSD([sQuery(id+"F0.wireOp",EDGE,"E9")])]})}),makeQuery(id+"F8.opExtrude","SWEPT_FACE",FACE,{"disambiguationData":[OSD([sQuery(id+"F7.wireOp",EDGE,"E46.6.5")])]})]});
            var Q56;
            Q56=makeQuery(id+"F8.boolean.opBoolean","INTERSECT",EDGE,{"derivedFrom":[makeQuery(id+"F1.opRevolve","SWEPT_FACE",FACE,{"disambiguationData":[OSD([sQuery(id+"F0.wireOp",EDGE,"E8")])]}),makeQuery(id+"F8.opExtrude","SWEPT_FACE",FACE,{"disambiguationData":[OSD([sQuery(id+"F7.wireOp",EDGE,"E46.6.0")])]})]});
            var Q57;
            Q57=makeQuery(id+"F8.boolean.opBoolean","INTERSECT",EDGE,{"derivedFrom":[makeQuery(id+"F1.opRevolve","SWEPT_FACE",FACE,{"disambiguationData":[OSD([sQuery(id+"F0.wireOp",EDGE,"E8")])]}),makeQuery(id+"F8.opExtrude","SWEPT_FACE",FACE,{"disambiguationData":[OSD([sQuery(id+"F7.wireOp",EDGE,"E46.6.5")])]})]});
            var Q58;
            Q58=makeQuery(id+"F8.boolean.opBoolean","INTERSECT",EDGE,{"derivedFrom":[makeQuery(id+"F1.opRevolve","SWEPT_FACE",FACE,{"disambiguationData":[OSD([sQuery(id+"F0.wireOp",EDGE,"E8")])]}),makeQuery(id+"F8.opExtrude","SWEPT_FACE",FACE,{"disambiguationData":[OSD([sQuery(id+"F7.wireOp",EDGE,"E46.6.1")])]})]});
            var Q59;
            Q59=makeQuery(id+"F8.boolean.opBoolean","INTERSECT",EDGE,{"derivedFrom":[makeQuery(id+"F4.boolean.opBoolean","SPLIT",FACE,{"disambiguationData":[TD([makeQuery(id+"F4.opExtrude","SWEPT_FACE",FACE,{"disambiguationData":[OSD([sQuery(id+"F3.wireOp",EDGE,"E33.3.0")])]})])],"derivedFrom":makeQuery(id+"F1.opRevolve","SWEPT_FACE",FACE,{"disambiguationData":[OSD([sQuery(id+"F0.wireOp",EDGE,"E9")])]})}),makeQuery(id+"F8.opExtrude","SWEPT_FACE",FACE,{"disambiguationData":[OSD([sQuery(id+"F7.wireOp",EDGE,"E46.6.1")])]})]});
            var Q60;
            Q60=makeQuery(id+"F8.boolean.opBoolean","INTERSECT",EDGE,{"disambiguationData":[OD(0.0)],"derivedFrom":[makeQuery(id+"F4.boolean.opBoolean","SPLIT",FACE,{"disambiguationData":[TD([makeQuery(id+"F4.opExtrude","SWEPT_FACE",FACE,{"disambiguationData":[OSD([sQuery(id+"F3.wireOp",EDGE,"E33.3.5")])]})])],"derivedFrom":makeQuery(id+"F1.opRevolve","SWEPT_FACE",FACE,{"disambiguationData":[OSD([sQuery(id+"F0.wireOp",EDGE,"E9")])]})}),makeQuery(id+"F8.opExtrude","SWEPT_FACE",FACE,{"disambiguationData":[OSD([sQuery(id+"F7.wireOp",EDGE,"E46.7.3")])]})]});
            var Q61;
            Q61=makeQuery(id+"F8.boolean.opBoolean","INTERSECT",EDGE,{"derivedFrom":[makeQuery(id+"F1.opRevolve","SWEPT_FACE",FACE,{"disambiguationData":[OSD([sQuery(id+"F0.wireOp",EDGE,"E10")])]}),makeQuery(id+"F8.opExtrude","SWEPT_FACE",FACE,{"disambiguationData":[OSD([sQuery(id+"F7.wireOp",EDGE,"E46.7.3")])]})]});
            var Q62;
            Q62=makeQuery(id+"F8.boolean.opBoolean","INTERSECT",EDGE,{"derivedFrom":[makeQuery(id+"F4.boolean.opBoolean","SPLIT",FACE,{"disambiguationData":[TD([makeQuery(id+"F4.opExtrude","SWEPT_FACE",FACE,{"disambiguationData":[OSD([sQuery(id+"F3.wireOp",EDGE,"E33.3.5")])]})])],"derivedFrom":makeQuery(id+"F1.opRevolve","SWEPT_FACE",FACE,{"disambiguationData":[OSD([sQuery(id+"F0.wireOp",EDGE,"E9")])]})}),makeQuery(id+"F8.opExtrude","SWEPT_FACE",FACE,{"disambiguationData":[OSD([sQuery(id+"F7.wireOp",EDGE,"E46.7.4")])]})]});
            var Q63;
            Q63=makeQuery(id+"F8.boolean.opBoolean","INTERSECT",EDGE,{"disambiguationData":[OD(1.0)],"derivedFrom":[makeQuery(id+"F4.boolean.opBoolean","SPLIT",FACE,{"disambiguationData":[TD([makeQuery(id+"F4.opExtrude","SWEPT_FACE",FACE,{"disambiguationData":[OSD([sQuery(id+"F3.wireOp",EDGE,"E33.3.5")])]})])],"derivedFrom":makeQuery(id+"F1.opRevolve","SWEPT_FACE",FACE,{"disambiguationData":[OSD([sQuery(id+"F0.wireOp",EDGE,"E9")])]})}),makeQuery(id+"F8.opExtrude","SWEPT_FACE",FACE,{"disambiguationData":[OSD([sQuery(id+"F7.wireOp",EDGE,"E46.7.3")])]})]});
            var Q64;
            Q64=makeQuery(id+"F8.boolean.opBoolean","INTERSECT",EDGE,{"derivedFrom":[makeQuery(id+"F4.boolean.opBoolean","SPLIT",FACE,{"disambiguationData":[TD([makeQuery(id+"F4.opExtrude","SWEPT_FACE",FACE,{"disambiguationData":[OSD([sQuery(id+"F3.wireOp",EDGE,"E33.3.5")])]})])],"derivedFrom":makeQuery(id+"F1.opRevolve","SWEPT_FACE",FACE,{"disambiguationData":[OSD([sQuery(id+"F0.wireOp",EDGE,"E9")])]})}),makeQuery(id+"F8.opExtrude","SWEPT_FACE",FACE,{"disambiguationData":[OSD([sQuery(id+"F7.wireOp",EDGE,"E46.7.2")])]})]});
            var Q65;
            Q65=makeQuery(id+"F8.boolean.opBoolean","INTERSECT",EDGE,{"derivedFrom":[makeQuery(id+"F4.boolean.opBoolean","SPLIT",FACE,{"disambiguationData":[TD([makeQuery(id+"F4.opExtrude","SWEPT_FACE",FACE,{"disambiguationData":[OSD([sQuery(id+"F3.wireOp",EDGE,"E33.3.5")])]})])],"derivedFrom":makeQuery(id+"F1.opRevolve","SWEPT_FACE",FACE,{"disambiguationData":[OSD([sQuery(id+"F0.wireOp",EDGE,"E9")])]})}),makeQuery(id+"F8.opExtrude","SWEPT_FACE",FACE,{"disambiguationData":[OSD([sQuery(id+"F7.wireOp",EDGE,"E46.7.1")])]})]});
            var Q66;
            Q66=makeQuery(id+"F8.boolean.opBoolean","INTERSECT",EDGE,{"derivedFrom":[makeQuery(id+"F1.opRevolve","SWEPT_FACE",FACE,{"disambiguationData":[OSD([sQuery(id+"F0.wireOp",EDGE,"E8")])]}),makeQuery(id+"F8.opExtrude","SWEPT_FACE",FACE,{"disambiguationData":[OSD([sQuery(id+"F7.wireOp",EDGE,"E46.7.1")])]})]});
            var Q67;
            Q67=makeQuery(id+"F8.boolean.opBoolean","INTERSECT",EDGE,{"derivedFrom":[makeQuery(id+"F1.opRevolve","SWEPT_FACE",FACE,{"disambiguationData":[OSD([sQuery(id+"F0.wireOp",EDGE,"E8")])]}),makeQuery(id+"F8.opExtrude","SWEPT_FACE",FACE,{"disambiguationData":[OSD([sQuery(id+"F7.wireOp",EDGE,"E46.7.0")])]})]});
            var Q68;
            Q68=makeQuery(id+"F8.boolean.opBoolean","INTERSECT",EDGE,{"derivedFrom":[makeQuery(id+"F4.boolean.opBoolean","SPLIT",FACE,{"disambiguationData":[TD([makeQuery(id+"F4.opExtrude","SWEPT_FACE",FACE,{"disambiguationData":[OSD([sQuery(id+"F3.wireOp",EDGE,"E33.3.5")])]})])],"derivedFrom":makeQuery(id+"F1.opRevolve","SWEPT_FACE",FACE,{"disambiguationData":[OSD([sQuery(id+"F0.wireOp",EDGE,"E9")])]})}),makeQuery(id+"F8.opExtrude","SWEPT_FACE",FACE,{"disambiguationData":[OSD([sQuery(id+"F7.wireOp",EDGE,"E46.7.5")])]})]});
            var Q69;
            Q69=makeQuery(id+"F8.boolean.opBoolean","INTERSECT",EDGE,{"derivedFrom":[makeQuery(id+"F1.opRevolve","SWEPT_FACE",FACE,{"disambiguationData":[OSD([sQuery(id+"F0.wireOp",EDGE,"E8")])]}),makeQuery(id+"F8.opExtrude","SWEPT_FACE",FACE,{"disambiguationData":[OSD([sQuery(id+"F7.wireOp",EDGE,"E46.7.5")])]})]});
            var Q70;
            Q70=makeQuery(id+"F8.boolean.opBoolean","INTERSECT",EDGE,{"derivedFrom":[makeQuery(id+"F1.opRevolve","SWEPT_FACE",FACE,{"disambiguationData":[OSD([sQuery(id+"F0.wireOp",EDGE,"E8")])]}),makeQuery(id+"F8.opExtrude","SWEPT_FACE",FACE,{"disambiguationData":[OSD([sQuery(id+"F7.wireOp",EDGE,"E46.8.0")])]})]});
            var Q71;
            Q71=makeQuery(id+"F8.boolean.opBoolean","INTERSECT",EDGE,{"derivedFrom":[makeQuery(id+"F1.opRevolve","SWEPT_FACE",FACE,{"disambiguationData":[OSD([sQuery(id+"F0.wireOp",EDGE,"E8")])]}),makeQuery(id+"F8.opExtrude","SWEPT_FACE",FACE,{"disambiguationData":[OSD([sQuery(id+"F7.wireOp",EDGE,"E46.8.1")])]})]});
            var Q72;
            Q72=makeQuery(id+"F8.boolean.opBoolean","INTERSECT",EDGE,{"derivedFrom":[makeQuery(id+"F4.boolean.opBoolean","SPLIT",FACE,{"disambiguationData":[TD([makeQuery(id+"F4.opExtrude","SWEPT_FACE",FACE,{"disambiguationData":[OSD([sQuery(id+"F3.wireOp",EDGE,"E33.4.0")])]})])],"derivedFrom":makeQuery(id+"F1.opRevolve","SWEPT_FACE",FACE,{"disambiguationData":[OSD([sQuery(id+"F0.wireOp",EDGE,"E9")])]})}),makeQuery(id+"F8.opExtrude","SWEPT_FACE",FACE,{"disambiguationData":[OSD([sQuery(id+"F7.wireOp",EDGE,"E46.8.1")])]})]});
            var Q73;
            Q73=makeQuery(id+"F8.boolean.opBoolean","INTERSECT",EDGE,{"derivedFrom":[makeQuery(id+"F4.boolean.opBoolean","SPLIT",FACE,{"disambiguationData":[TD([makeQuery(id+"F4.opExtrude","SWEPT_FACE",FACE,{"disambiguationData":[OSD([sQuery(id+"F3.wireOp",EDGE,"E33.4.0")])]})])],"derivedFrom":makeQuery(id+"F1.opRevolve","SWEPT_FACE",FACE,{"disambiguationData":[OSD([sQuery(id+"F0.wireOp",EDGE,"E9")])]})}),makeQuery(id+"F8.opExtrude","SWEPT_FACE",FACE,{"disambiguationData":[OSD([sQuery(id+"F7.wireOp",EDGE,"E46.8.2")])]})]});
            var Q74;
            Q74=makeQuery(id+"F8.boolean.opBoolean","INTERSECT",EDGE,{"disambiguationData":[OD(0.0)],"derivedFrom":[makeQuery(id+"F4.boolean.opBoolean","SPLIT",FACE,{"disambiguationData":[TD([makeQuery(id+"F4.opExtrude","SWEPT_FACE",FACE,{"disambiguationData":[OSD([sQuery(id+"F3.wireOp",EDGE,"E33.4.0")])]})])],"derivedFrom":makeQuery(id+"F1.opRevolve","SWEPT_FACE",FACE,{"disambiguationData":[OSD([sQuery(id+"F0.wireOp",EDGE,"E9")])]})}),makeQuery(id+"F8.opExtrude","SWEPT_FACE",FACE,{"disambiguationData":[OSD([sQuery(id+"F7.wireOp",EDGE,"E46.8.3")])]})]});
            var Q75;
            Q75=makeQuery(id+"F8.boolean.opBoolean","INTERSECT",EDGE,{"derivedFrom":[makeQuery(id+"F1.opRevolve","SWEPT_FACE",FACE,{"disambiguationData":[OSD([sQuery(id+"F0.wireOp",EDGE,"E10")])]}),makeQuery(id+"F8.opExtrude","SWEPT_FACE",FACE,{"disambiguationData":[OSD([sQuery(id+"F7.wireOp",EDGE,"E46.8.3")])]})]});
            var Q76;
            Q76=makeQuery(id+"F8.boolean.opBoolean","INTERSECT",EDGE,{"derivedFrom":[makeQuery(id+"F4.boolean.opBoolean","SPLIT",FACE,{"disambiguationData":[TD([makeQuery(id+"F4.opExtrude","SWEPT_FACE",FACE,{"disambiguationData":[OSD([sQuery(id+"F3.wireOp",EDGE,"E33.4.0")])]})])],"derivedFrom":makeQuery(id+"F1.opRevolve","SWEPT_FACE",FACE,{"disambiguationData":[OSD([sQuery(id+"F0.wireOp",EDGE,"E9")])]})}),makeQuery(id+"F8.opExtrude","SWEPT_FACE",FACE,{"disambiguationData":[OSD([sQuery(id+"F7.wireOp",EDGE,"E46.8.4")])]})]});
            var Q77;
            Q77=makeQuery(id+"F8.boolean.opBoolean","INTERSECT",EDGE,{"disambiguationData":[OD(1.0)],"derivedFrom":[makeQuery(id+"F4.boolean.opBoolean","SPLIT",FACE,{"disambiguationData":[TD([makeQuery(id+"F4.opExtrude","SWEPT_FACE",FACE,{"disambiguationData":[OSD([sQuery(id+"F3.wireOp",EDGE,"E33.4.0")])]})])],"derivedFrom":makeQuery(id+"F1.opRevolve","SWEPT_FACE",FACE,{"disambiguationData":[OSD([sQuery(id+"F0.wireOp",EDGE,"E9")])]})}),makeQuery(id+"F8.opExtrude","SWEPT_FACE",FACE,{"disambiguationData":[OSD([sQuery(id+"F7.wireOp",EDGE,"E46.8.3")])]})]});
            var Q78;
            Q78=makeQuery(id+"F8.boolean.opBoolean","INTERSECT",EDGE,{"derivedFrom":[makeQuery(id+"F4.boolean.opBoolean","SPLIT",FACE,{"disambiguationData":[TD([makeQuery(id+"F4.opExtrude","SWEPT_FACE",FACE,{"disambiguationData":[OSD([sQuery(id+"F3.wireOp",EDGE,"E33.4.0")])]})])],"derivedFrom":makeQuery(id+"F1.opRevolve","SWEPT_FACE",FACE,{"disambiguationData":[OSD([sQuery(id+"F0.wireOp",EDGE,"E9")])]})}),makeQuery(id+"F8.opExtrude","SWEPT_FACE",FACE,{"disambiguationData":[OSD([sQuery(id+"F7.wireOp",EDGE,"E46.8.5")])]})]});
            var Q79;
            Q79=makeQuery(id+"F8.boolean.opBoolean","INTERSECT",EDGE,{"derivedFrom":[makeQuery(id+"F1.opRevolve","SWEPT_FACE",FACE,{"disambiguationData":[OSD([sQuery(id+"F0.wireOp",EDGE,"E8")])]}),makeQuery(id+"F8.opExtrude","SWEPT_FACE",FACE,{"disambiguationData":[OSD([sQuery(id+"F7.wireOp",EDGE,"E46.8.5")])]})]});
            var Q80;
            Q80=makeQuery(id+"F8.boolean.opBoolean","INTERSECT",EDGE,{"derivedFrom":[makeQuery(id+"F1.opRevolve","SWEPT_FACE",FACE,{"disambiguationData":[OSD([sQuery(id+"F0.wireOp",EDGE,"E8")])]}),makeQuery(id+"F8.opExtrude","SWEPT_FACE",FACE,{"disambiguationData":[OSD([sQuery(id+"F7.wireOp",EDGE,"E46.9.0")])]})]});
            var Q81;
            Q81=makeQuery(id+"F8.boolean.opBoolean","INTERSECT",EDGE,{"derivedFrom":[makeQuery(id+"F1.opRevolve","SWEPT_FACE",FACE,{"disambiguationData":[OSD([sQuery(id+"F0.wireOp",EDGE,"E8")])]}),makeQuery(id+"F8.opExtrude","SWEPT_FACE",FACE,{"disambiguationData":[OSD([sQuery(id+"F7.wireOp",EDGE,"E46.9.1")])]})]});
            var Q82;
            Q82=makeQuery(id+"F8.boolean.opBoolean","INTERSECT",EDGE,{"derivedFrom":[makeQuery(id+"F4.boolean.opBoolean","SPLIT",FACE,{"disambiguationData":[TD([makeQuery(id+"F4.opExtrude","SWEPT_FACE",FACE,{"disambiguationData":[OSD([sQuery(id+"F3.wireOp",EDGE,"E25.MirrorCS")])]})])],"derivedFrom":makeQuery(id+"F1.opRevolve","SWEPT_FACE",FACE,{"disambiguationData":[OSD([sQuery(id+"F0.wireOp",EDGE,"E9")])]})}),makeQuery(id+"F8.opExtrude","SWEPT_FACE",FACE,{"disambiguationData":[OSD([sQuery(id+"F7.wireOp",EDGE,"E46.9.1")])]})]});
            var Q83;
            Q83=makeQuery(id+"F8.boolean.opBoolean","INTERSECT",EDGE,{"derivedFrom":[makeQuery(id+"F4.boolean.opBoolean","SPLIT",FACE,{"disambiguationData":[TD([makeQuery(id+"F4.opExtrude","SWEPT_FACE",FACE,{"disambiguationData":[OSD([sQuery(id+"F3.wireOp",EDGE,"E25.MirrorCS")])]})])],"derivedFrom":makeQuery(id+"F1.opRevolve","SWEPT_FACE",FACE,{"disambiguationData":[OSD([sQuery(id+"F0.wireOp",EDGE,"E9")])]})}),makeQuery(id+"F8.opExtrude","SWEPT_FACE",FACE,{"disambiguationData":[OSD([sQuery(id+"F7.wireOp",EDGE,"E46.9.2")])]})]});
            var Q84;
            Q84=makeQuery(id+"F8.boolean.opBoolean","INTERSECT",EDGE,{"disambiguationData":[OD(0.0)],"derivedFrom":[makeQuery(id+"F4.boolean.opBoolean","SPLIT",FACE,{"disambiguationData":[TD([makeQuery(id+"F4.opExtrude","SWEPT_FACE",FACE,{"disambiguationData":[OSD([sQuery(id+"F3.wireOp",EDGE,"E25.MirrorCS")])]})])],"derivedFrom":makeQuery(id+"F1.opRevolve","SWEPT_FACE",FACE,{"disambiguationData":[OSD([sQuery(id+"F0.wireOp",EDGE,"E9")])]})}),makeQuery(id+"F8.opExtrude","SWEPT_FACE",FACE,{"disambiguationData":[OSD([sQuery(id+"F7.wireOp",EDGE,"E46.9.3")])]})]});
            var Q85;
            Q85=makeQuery(id+"F8.boolean.opBoolean","INTERSECT",EDGE,{"derivedFrom":[makeQuery(id+"F1.opRevolve","SWEPT_FACE",FACE,{"disambiguationData":[OSD([sQuery(id+"F0.wireOp",EDGE,"E10")])]}),makeQuery(id+"F8.opExtrude","SWEPT_FACE",FACE,{"disambiguationData":[OSD([sQuery(id+"F7.wireOp",EDGE,"E46.9.3")])]})]});
            var Q86;
            Q86=makeQuery(id+"F8.boolean.opBoolean","INTERSECT",EDGE,{"derivedFrom":[makeQuery(id+"F4.boolean.opBoolean","SPLIT",FACE,{"disambiguationData":[TD([makeQuery(id+"F4.opExtrude","SWEPT_FACE",FACE,{"disambiguationData":[OSD([sQuery(id+"F3.wireOp",EDGE,"E25.MirrorCS")])]})])],"derivedFrom":makeQuery(id+"F1.opRevolve","SWEPT_FACE",FACE,{"disambiguationData":[OSD([sQuery(id+"F0.wireOp",EDGE,"E9")])]})}),makeQuery(id+"F8.opExtrude","SWEPT_FACE",FACE,{"disambiguationData":[OSD([sQuery(id+"F7.wireOp",EDGE,"E46.9.4")])]})]});
            var Q87;
            Q87=makeQuery(id+"F8.boolean.opBoolean","INTERSECT",EDGE,{"disambiguationData":[OD(1.0)],"derivedFrom":[makeQuery(id+"F4.boolean.opBoolean","SPLIT",FACE,{"disambiguationData":[TD([makeQuery(id+"F4.opExtrude","SWEPT_FACE",FACE,{"disambiguationData":[OSD([sQuery(id+"F3.wireOp",EDGE,"E25.MirrorCS")])]})])],"derivedFrom":makeQuery(id+"F1.opRevolve","SWEPT_FACE",FACE,{"disambiguationData":[OSD([sQuery(id+"F0.wireOp",EDGE,"E9")])]})}),makeQuery(id+"F8.opExtrude","SWEPT_FACE",FACE,{"disambiguationData":[OSD([sQuery(id+"F7.wireOp",EDGE,"E46.9.3")])]})]});
            var Q88;
            Q88=makeQuery(id+"F8.boolean.opBoolean","INTERSECT",EDGE,{"derivedFrom":[makeQuery(id+"F1.opRevolve","SWEPT_FACE",FACE,{"disambiguationData":[OSD([sQuery(id+"F0.wireOp",EDGE,"E8")])]}),makeQuery(id+"F8.opExtrude","SWEPT_FACE",FACE,{"disambiguationData":[OSD([sQuery(id+"F7.wireOp",EDGE,"E46.9.5")])]})]});
            var Q89;
            Q89=makeQuery(id+"F8.boolean.opBoolean","INTERSECT",EDGE,{"derivedFrom":[makeQuery(id+"F4.boolean.opBoolean","SPLIT",FACE,{"disambiguationData":[TD([makeQuery(id+"F4.opExtrude","SWEPT_FACE",FACE,{"disambiguationData":[OSD([sQuery(id+"F3.wireOp",EDGE,"E25.MirrorCS")])]})])],"derivedFrom":makeQuery(id+"F1.opRevolve","SWEPT_FACE",FACE,{"disambiguationData":[OSD([sQuery(id+"F0.wireOp",EDGE,"E9")])]})}),makeQuery(id+"F8.opExtrude","SWEPT_FACE",FACE,{"disambiguationData":[OSD([sQuery(id+"F7.wireOp",EDGE,"E46.9.5")])]})]});
            var Q90;
            Q90=makeQuery(id+"F8.boolean.opBoolean","INTERSECT",EDGE,{"derivedFrom":[makeQuery(id+"F1.opRevolve","SWEPT_FACE",FACE,{"disambiguationData":[OSD([sQuery(id+"F0.wireOp",EDGE,"E8")])]}),makeQuery(id+"F8.opExtrude","SWEPT_FACE",FACE,{"disambiguationData":[OSD([sQuery(id+"F7.wireOp",EDGE,"E43")])]})]});
            var Q91;
            Q91=makeQuery(id+"F8.boolean.opBoolean","INTERSECT",EDGE,{"derivedFrom":[makeQuery(id+"F1.opRevolve","SWEPT_FACE",FACE,{"disambiguationData":[OSD([sQuery(id+"F0.wireOp",EDGE,"E8")])]}),makeQuery(id+"F8.opExtrude","SWEPT_FACE",FACE,{"disambiguationData":[OSD([sQuery(id+"F7.wireOp",EDGE,"E40")])]})]});
            var Q92;
            Q92=makeQuery(id+"F8.boolean.opBoolean","INTERSECT",EDGE,{"derivedFrom":[makeQuery(id+"F4.boolean.opBoolean","SPLIT",FACE,{"disambiguationData":[TD([makeQuery(id+"F4.opExtrude","SWEPT_FACE",FACE,{"disambiguationData":[OSD([sQuery(id+"F3.wireOp",EDGE,"E24")])]})])],"derivedFrom":makeQuery(id+"F1.opRevolve","SWEPT_FACE",FACE,{"disambiguationData":[OSD([sQuery(id+"F0.wireOp",EDGE,"E9")])]})}),makeQuery(id+"F8.opExtrude","SWEPT_FACE",FACE,{"disambiguationData":[OSD([sQuery(id+"F7.wireOp",EDGE,"E40")])]})]});
            var Q93;
            Q93=makeQuery(id+"F8.boolean.opBoolean","INTERSECT",EDGE,{"derivedFrom":[makeQuery(id+"F1.opRevolve","SWEPT_FACE",FACE,{"disambiguationData":[OSD([sQuery(id+"F0.wireOp",EDGE,"E10")])]}),makeQuery(id+"F8.opExtrude","SWEPT_FACE",FACE,{"disambiguationData":[OSD([sQuery(id+"F7.wireOp",EDGE,"E42")])]})]});
            var Q94;
            Q94=makeQuery(id+"F8.boolean.opBoolean","INTERSECT",EDGE,{"disambiguationData":[OD(0.0)],"derivedFrom":[makeQuery(id+"F4.boolean.opBoolean","SPLIT",FACE,{"disambiguationData":[TD([makeQuery(id+"F4.opExtrude","SWEPT_FACE",FACE,{"disambiguationData":[OSD([sQuery(id+"F3.wireOp",EDGE,"E24")])]})])],"derivedFrom":makeQuery(id+"F1.opRevolve","SWEPT_FACE",FACE,{"disambiguationData":[OSD([sQuery(id+"F0.wireOp",EDGE,"E9")])]})}),makeQuery(id+"F8.opExtrude","SWEPT_FACE",FACE,{"disambiguationData":[OSD([sQuery(id+"F7.wireOp",EDGE,"E42")])]})]});
            var Q95;
            Q95=makeQuery(id+"F8.boolean.opBoolean","INTERSECT",EDGE,{"derivedFrom":[makeQuery(id+"F4.boolean.opBoolean","SPLIT",FACE,{"disambiguationData":[TD([makeQuery(id+"F4.opExtrude","SWEPT_FACE",FACE,{"disambiguationData":[OSD([sQuery(id+"F3.wireOp",EDGE,"E24")])]})])],"derivedFrom":makeQuery(id+"F1.opRevolve","SWEPT_FACE",FACE,{"disambiguationData":[OSD([sQuery(id+"F0.wireOp",EDGE,"E9")])]})}),makeQuery(id+"F8.opExtrude","SWEPT_FACE",FACE,{"disambiguationData":[OSD([sQuery(id+"F7.wireOp",EDGE,"E44")])]})]});
            var Q96;
            Q96=makeQuery(id+"F8.boolean.opBoolean","INTERSECT",EDGE,{"derivedFrom":[makeQuery(id+"F1.opRevolve","SWEPT_FACE",FACE,{"disambiguationData":[OSD([sQuery(id+"F0.wireOp",EDGE,"E8")])]}),makeQuery(id+"F8.opExtrude","SWEPT_FACE",FACE,{"disambiguationData":[OSD([sQuery(id+"F7.wireOp",EDGE,"E41.MirrorCS")])]})]});
            var Q97;
            Q97=makeQuery(id+"F8.boolean.opBoolean","INTERSECT",EDGE,{"derivedFrom":[makeQuery(id+"F4.boolean.opBoolean","SPLIT",FACE,{"disambiguationData":[TD([makeQuery(id+"F4.opExtrude","SWEPT_FACE",FACE,{"disambiguationData":[OSD([sQuery(id+"F3.wireOp",EDGE,"E24")])]})])],"derivedFrom":makeQuery(id+"F1.opRevolve","SWEPT_FACE",FACE,{"disambiguationData":[OSD([sQuery(id+"F0.wireOp",EDGE,"E9")])]})}),makeQuery(id+"F8.opExtrude","SWEPT_FACE",FACE,{"disambiguationData":[OSD([sQuery(id+"F7.wireOp",EDGE,"E41.MirrorCS")])]})]});
            var Q98;
            Q98=makeQuery(id+"F8.boolean.opBoolean","INTERSECT",EDGE,{"disambiguationData":[OD(1.0)],"derivedFrom":[makeQuery(id+"F4.boolean.opBoolean","SPLIT",FACE,{"disambiguationData":[TD([makeQuery(id+"F4.opExtrude","SWEPT_FACE",FACE,{"disambiguationData":[OSD([sQuery(id+"F3.wireOp",EDGE,"E24")])]})])],"derivedFrom":makeQuery(id+"F1.opRevolve","SWEPT_FACE",FACE,{"disambiguationData":[OSD([sQuery(id+"F0.wireOp",EDGE,"E9")])]})}),makeQuery(id+"F8.opExtrude","SWEPT_FACE",FACE,{"disambiguationData":[OSD([sQuery(id+"F7.wireOp",EDGE,"E42")])]})]});
            var Q99;
            Q99=makeQuery(id+"F8.boolean.opBoolean","INTERSECT",EDGE,{"derivedFrom":[makeQuery(id+"F4.boolean.opBoolean","SPLIT",FACE,{"disambiguationData":[TD([makeQuery(id+"F4.opExtrude","SWEPT_FACE",FACE,{"disambiguationData":[OSD([sQuery(id+"F3.wireOp",EDGE,"E24")])]})])],"derivedFrom":makeQuery(id+"F1.opRevolve","SWEPT_FACE",FACE,{"disambiguationData":[OSD([sQuery(id+"F0.wireOp",EDGE,"E9")])]})}),makeQuery(id+"F8.opExtrude","SWEPT_FACE",FACE,{"disambiguationData":[OSD([sQuery(id+"F7.wireOp",EDGE,"E45")])]})]});
            fillet(context, id + "F11", {"entities" : qUnion([Q0, Q1, Q2, Q3, Q4, Q5, Q6, Q7, Q8, Q9, Q10, Q11, Q12, Q13, Q14, Q15, Q16, Q17, Q18, Q19, Q20, Q21, Q22, Q23, Q24, Q25, Q26, Q27, Q28, Q29, Q30, Q31, Q32, Q33, Q34, Q35, Q36, Q37, Q38, Q39, Q40, Q41, Q42, Q43, Q44, Q45, Q46, Q47, Q48, Q49, Q50, Q51, Q52, Q53, Q54, Q55, Q56, Q57, Q58, Q59, Q60, Q61, Q62, Q63, Q64, Q65, Q66, Q67, Q68, Q69, Q70, Q71, Q72, Q73, Q74, Q75, Q76, Q77, Q78, Q79, Q80, Q81, Q82, Q83, Q84, Q85, Q86, Q87, Q88, Q89, Q90, Q91, Q92, Q93, Q94, Q95, Q96, Q97, Q98, Q99]), "radius" : 2.5 * mm, "tangentPropagation" : true, "allowEdgeOverflow" : false});
        }
        {
            var Q0;
            Q0=makeQuery(id+"F1.opRevolve","SWEPT_EDGE",EDGE,{"disambiguationData":[OSD([sQuery(id+"F0.wireOp",EDGE,"E4"),sQuery(id+"F0.wireOp",EDGE,"E7")])]});
            var Q1;
            Q1=makeQuery(id+"F1.opRevolve","SWEPT_EDGE",EDGE,{"disambiguationData":[OSD([sQuery(id+"F0.wireOp",EDGE,"E3"),sQuery(id+"F0.wireOp",EDGE,"E4")])]});
            fillet(context, id + "F12", {"entities" : qUnion([Q0, Q1]), "radius" : 5 * mm, "tangentPropagation" : true, "allowEdgeOverflow" : false});
        }
        {
            var Q0;
            Q0=makeQuery(id+"F1.opRevolve","SWEPT_FACE",FACE,{"disambiguationData":[OSD([sQuery(id+"F0.wireOp",EDGE,"E21")])]});
            var sketch = newSketch(context, id + "F13", { "sketchPlane" : qUnion([Q0])});
            skCircle(sketch, "E47", {"center": v(0, 0) * mm, "radius": 41.03 * mm});
            skSolve(sketch);
        }
        {
            var Q0;
            Q0 = qSketchRegion(id + "F13", true);
            extrude(context, id + "F14", {"entities" : qUnion([Q0]), "operationType" : NewBodyOperationType.ADD, "oppositeDirection" : true, "depth" : 73 * mm, "offsetDistance" : 25 * mm});
        }
        {
            var Q0;
            Q0=makeQuery(id+"F14.boolean.opBoolean","INTERSECT",EDGE,{"derivedFrom":[makeQuery(id+"F1.opRevolve","SWEPT_FACE",FACE,{"disambiguationData":[OSD([sQuery(id+"F0.wireOp",EDGE,"E10")])]}),makeQuery(id+"F14.opExtrude","SWEPT_FACE",FACE,{"disambiguationData":[OSD([sQuery(id+"F13.wireOp",EDGE,"E47")])]})]});
            fillet(context, id + "F15", {"entities" : qUnion([Q0]), "radius" : 7 * mm, "tangentPropagation" : true, "allowEdgeOverflow" : false});
        }
        {
            var Q0;
            Q0=qCreatedBy(id+"F2.planeOp",FACE);
            var sketch = newSketch(context, id + "F16", { "sketchPlane" : qUnion([Q0])});
            skCircle(sketch, "E48", {"center": v(0, 57.56) * mm, "radius": 14.8 * mm});
            skCircle(sketch, "E49.1.0", {"center": v(-54.74, 17.79) * mm, "radius": 14.8 * mm});
            skCircle(sketch, "E49.2.0", {"center": v(-33.83, -46.57) * mm, "radius": 14.8 * mm});
            skCircle(sketch, "E49.3.0", {"center": v(33.83, -46.57) * mm, "radius": 14.8 * mm});
            skCircle(sketch, "E49.4.0", {"center": v(54.74, 17.79) * mm, "radius": 14.8 * mm});
            skPoint(sketch, "E49.center", {"position": v(0, 0) * mm});
            skSolve(sketch);
        }
        {
            var Q0;
            Q0 = qSketchRegion(id + "F16", true);
            extrude(context, id + "F17", {"entities" : qUnion([Q0]), "operationType" : NewBodyOperationType.REMOVE, "oppositeDirection" : true, "depth" : 53 * mm, "offsetDistance" : 25 * mm});
        }
        {
            var Q0;
            Q0=makeQuery(id+"F17.boolean.opBoolean","COPY",FACE,{"derivedFrom":makeQuery(id+"F17.opExtrude","CAP_FACE",FACE,{"disambiguationData":[OSD([sQuery(id+"F16.wireOp",EDGE,"E48")])],"isStart":false})});
            var sketch = newSketch(context, id + "F18", { "sketchPlane" : qUnion([Q0])});
            skCircle(sketch, "E50.0.0", {"center": v(0, 57.56) * mm, "radius": 14.8 * mm, "construction": true});
            skCircle(sketch, "E51", {"center": v(0, 57.56) * mm, "radius": 12.71 * mm});
            skSolve(sketch);
        }
        {
            var Q0;
            Q0 = qSketchRegion(id + "F18", true);
            extrude(context, id + "F19", {"entities" : qUnion([Q0]), "depth" : 38.9 * mm, "offsetDistance" : 25 * mm});
        }
        {
            var Q0;
            Q0=makeQuery(id+"F19.opExtrude","CAP_EDGE",EDGE,{"disambiguationData":[OSD([sQuery(id+"F18.wireOp",EDGE,"E51")])],"isStart":false});
            fillet(context, id + "F20", {"entities" : qUnion([Q0]), "radius" : 5 * mm, "tangentPropagation" : true, "allowEdgeOverflow" : false});
        }
        {
            var Q0;
            Q0=makeQuery(id+"F19.opExtrude","CAP_FACE",FACE,{"disambiguationData":[OSD([sQuery(id+"F18.wireOp",EDGE,"E51")])],"isStart":false});
            var sketch = newSketch(context, id + "F21", { "sketchPlane" : qUnion([Q0])});
            skCircle(sketch, "E52.cCircle", {"center": v(0, 57.56) * mm, "radius": 11.06 * mm, "construction": true});
            skLineSegment(sketch, "E52.0", {"start": v(-6.38, 68.62) * mm, "end": v(6.38, 68.62) * mm});
            skLineSegment(sketch, "E52.1", {"start": v(6.38, 68.62) * mm, "end": v(12.77, 57.56) * mm});
            skLineSegment(sketch, "E52.2", {"start": v(12.77, 57.56) * mm, "end": v(6.38, 46.5) * mm});
            skLineSegment(sketch, "E52.3", {"start": v(6.38, 46.5) * mm, "end": v(-6.38, 46.5) * mm});
            skLineSegment(sketch, "E52.4", {"start": v(-6.38, 46.5) * mm, "end": v(-12.77, 57.56) * mm});
            skLineSegment(sketch, "E52.5", {"start": v(-12.77, 57.56) * mm, "end": v(-6.38, 68.62) * mm});
            skPoint(sketch, "E52.0.midPoint", {"position": v(0, 68.62) * mm});
            skSolve(sketch);
        }
        {
            var Q0;
            Q0 = qSketchRegion(id + "F21", true);
            extrude(context, id + "F22", {"entities" : qUnion([Q0]), "operationType" : NewBodyOperationType.INTERSECT, "oppositeDirection" : true, "depth" : 25 * mm, "offsetDistance" : 25 * mm});
        }
        {
            var Q0;
            Q0=makeQuery(id+"F19.opExtrude","SWEPT_BODY",BODY,{"disambiguationData":[OSD([sQuery(id+"F18.wireOp",EDGE,"E51")])]});
            var Q1;
            Q1=sQuery(id+"F0.wireOp",EDGE,"E0");
            circularPattern(context, id + "F23", {"entities" : qUnion([Q0]), "axis" : qUnion([Q1]), "angle" : 360 * degree, "instanceCount" : 5, "equalSpace" : true, "computeTransformsWithoutBuiltin" : true});
        }
        {
            var Q0;
            Q0=qCreatedBy(makeId("Right.planeOp"),FACE);
            var sketch = newSketch(context, id + "F24", { "sketchPlane" : qUnion([Q0])});
            skLineSegment(sketch, "E53", {"start": v(-194.89, 243.12) * mm, "end": v(-187.72, 236.13) * mm});
            skLineSegment(sketch, "E54", {"start": v(-187.72, 236.13) * mm, "end": v(-187.72, 227.4) * mm});
            skLineSegment(sketch, "E55", {"start": v(-187.72, 227.4) * mm, "end": v(-178.2, 227.4) * mm});
            skLineSegment(sketch, "E56", {"start": v(-178.2, 227.4) * mm, "end": v(-178.2, 251.4) * mm});
            skLineSegment(sketch, "E57", {"start": v(-178.2, 251.4) * mm, "end": v(-194.89, 243.12) * mm});
            skSolve(sketch);
        }
        {
            var Q0;
            Q0 = qSketchRegion(id + "F24", true);
            var Q1;
            Q1=sQuery(id+"F0.wireOp",EDGE,"E0");
            revolve(context, id + "F25", {"operationType" : NewBodyOperationType.ADD, "entities" : qUnion([Q0]), "axis" : qUnion([Q1]), "revolveType" : RevolveType.FULL});
        }
        {
            var Q0;
            Q0=qCreatedBy(makeId("Right.planeOp"),FACE);
            var sketch = newSketch(context, id + "F26", { "sketchPlane" : qUnion([Q0])});
            skLineSegment(sketch, "E58.0", {"start": v(-208.2, 270) * mm, "end": v(-208.2, 265.42) * mm});
            skFitSpline(sketch, "E59", {"points": [v(-208.2, 270) * mm, v(-257.68, 0) * mm], "startDerivative": vector(-112.08, -111.58) * mm, "endDerivative": vector(-9.64, -270.17) * mm});
            skFitSpline(sketch, "E60", {"points": [v(-208.2, 265.42) * mm, v(-252.69, 0) * mm], "startDerivative": vector(-106.73, -136.38) * mm, "endDerivative": vector(-14.99, -233.77) * mm});
            skLineSegment(sketch, "E61", {"start": v(-252.69, 0) * mm, "end": v(-257.68, 0) * mm});
            skSolve(sketch);
        }
        {
            var Q0;
            Q0 = qSketchRegion(id + "F26", true);
            var Q1;
            Q1=sQuery(id+"F0.wireOp",EDGE,"E0");
            revolve(context, id + "F27", {"entities" : qUnion([Q0]), "axis" : qUnion([Q1]), "revolveType" : RevolveType.FULL});
        }
    });
